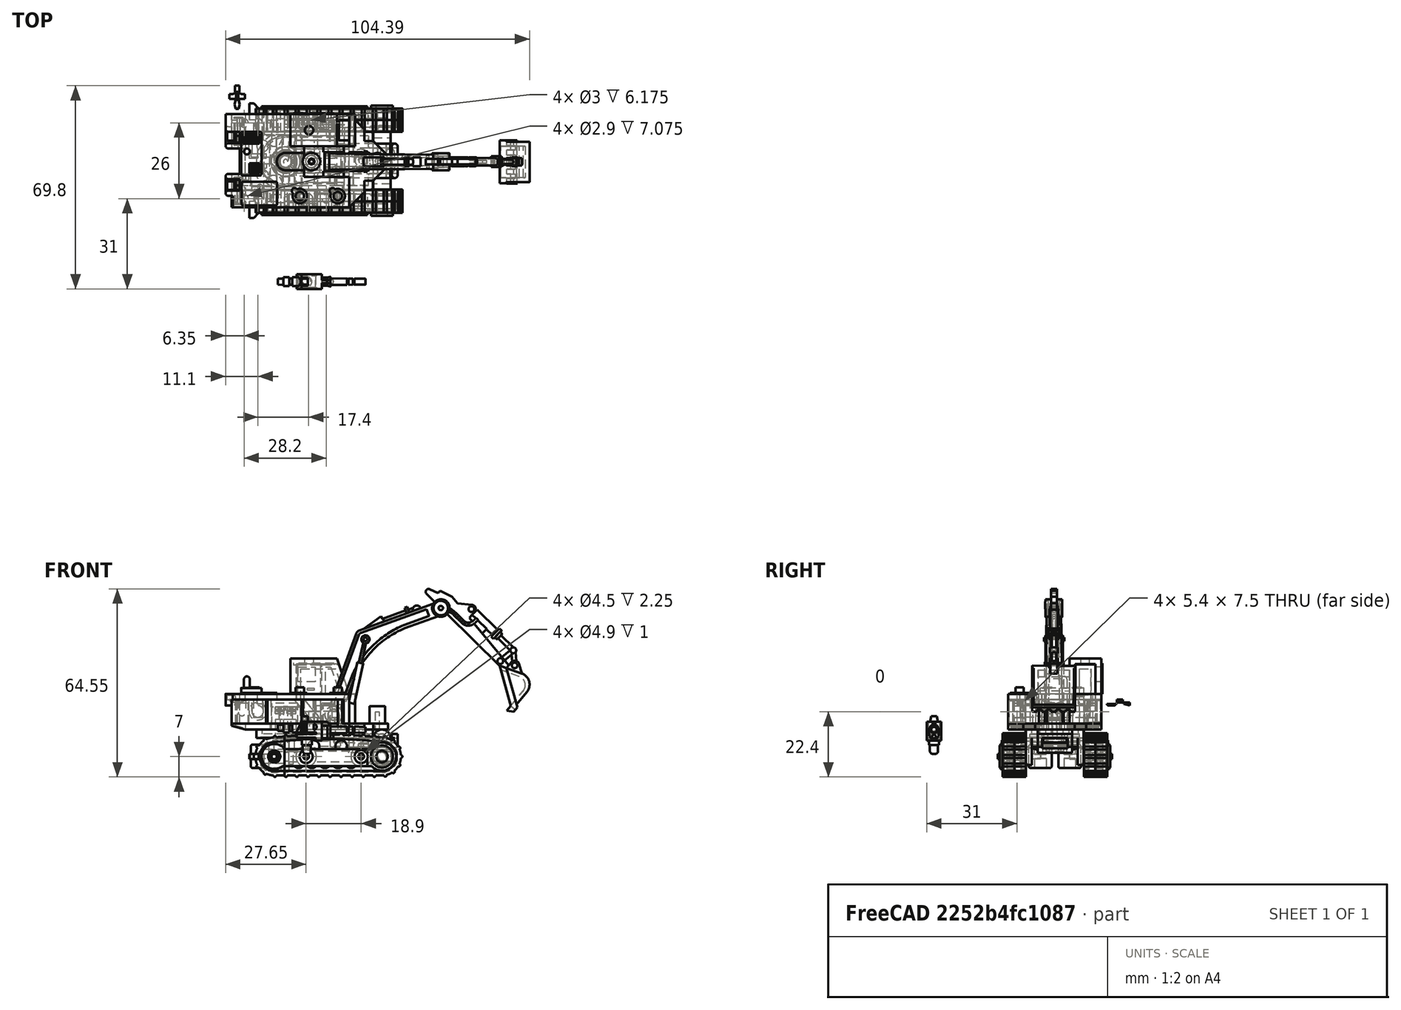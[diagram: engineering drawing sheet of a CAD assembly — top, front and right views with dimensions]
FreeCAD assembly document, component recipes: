
FREECAD ASSEMBLY — COMPONENT RECIPES ("Scavanger")

This assembly document has 15 components, labeled P0..P14 below (a component is one placed body or linked part). 15 of them carry a construction recipe — the FreeCAD feature program that regenerates the part from scratch, quoted from this document or its linked companion documents; the rest are supplied as boundary geometry only. No exploded tour is included for this assembly.
NOTE — this tour is split across 4 documents so each fits a 32k-token context. This is document 1: the component sections continue in the remaining 3 documents, each repeating the header above.
COMPONENT P0 — recipe-attached ("Rear_Torso", modeled in this document).
Construction recipe (the document's own serialized feature program — sketch geometry with constraints, then the solid features built on it; lengths are millimeters unless a unit is written):

FEATURE [Sketcher::SketchObject] Sketch
  ArcFitTolerance = 1e-06
  AttachmentSupport = -> [XY_Plane]
  FullyConstrained = true
  MakeInternals = false
  MapMode = 5
  sketch-geometry (43):
    g0: LineSegment StartX=0 StartY=0 StartZ=0 EndX=44.5 EndY=0 EndZ=0
    g1: LineSegment StartX=44.5 StartY=0 StartZ=0 EndX=44.5 EndY=-11 EndZ=0
    g2: LineSegment StartX=44.5 StartY=-11 StartZ=0 EndX=27 EndY=-11 EndZ=0
    g3: LineSegment StartX=27 StartY=-11 StartZ=0 EndX=27 EndY=-13.25 EndZ=0
    g4: LineSegment StartX=27 StartY=-13.25 StartZ=0 EndX=20.6 EndY=-13.25 EndZ=0
    g5: ArcOfCircle CenterX=20.6 CenterY=-16.25 CenterZ=0 NormalX=0 NormalY=0 NormalZ=1 AngleXU=0 Radius=3 StartAngle=1.5708 EndAngle=4.71239
    g6: LineSegment StartX=20.6 StartY=-19.25 StartZ=0 EndX=27 EndY=-19.25 EndZ=0
    g7: LineSegment StartX=27 StartY=-19.25 StartZ=0 EndX=27 EndY=-21.5 EndZ=0
    g8: LineSegment StartX=27 StartY=-21.5 StartZ=0 EndX=42.5 EndY=-21.5 EndZ=0
    g9: LineSegment StartX=42.5 StartY=-21.5 StartZ=0 EndX=42.5 EndY=-32 EndZ=0
    g10: LineSegment StartX=42.5 StartY=-32 StartZ=0 EndX=2.5 EndY=-32 EndZ=0
    g11: LineSegment StartX=2.5 StartY=-32 StartZ=0 EndX=2.5 EndY=-28 EndZ=0
    g12: LineSegment StartX=2.5 StartY=-28 StartZ=0 EndX=0.875 EndY=-28 EndZ=0
    g13: ArcOfCircle CenterX=0.875 CenterY=-27.125 CenterZ=0 NormalX=0 NormalY=0 NormalZ=1 AngleXU=0 Radius=0.875 StartAngle=1.5708 EndAngle=4.71239
    g14: LineSegment StartX=0.875 StartY=-26.25 StartZ=0 EndX=4.8 EndY=-26.25 EndZ=0
    g15: LineSegment StartX=4.8 StartY=-26.25 StartZ=0 EndX=4.8 EndY=-22.25 EndZ=0
    g16: LineSegment StartX=4.8 StartY=-22.25 StartZ=0 EndX=0.875 EndY=-22.25 EndZ=0
    g17: ArcOfCircle CenterX=0.875 CenterY=-21.375 CenterZ=0 NormalX=0 NormalY=0 NormalZ=1 AngleXU=0 Radius=0.875 StartAngle=1.5708 EndAngle=4.71239
    g18: LineSegment StartX=0.875 StartY=-20.5 StartZ=0 EndX=4.8 EndY=-20.5 EndZ=0
    g19: LineSegment StartX=4.8 StartY=-20.5 StartZ=0 EndX=4.8 EndY=-11.75 EndZ=0
    g20: LineSegment StartX=4.8 StartY=-11.75 StartZ=0 EndX=0.875 EndY=-11.75 EndZ=0
    g21: ArcOfCircle CenterX=0.875 CenterY=-10.875 CenterZ=0 NormalX=0 NormalY=0 NormalZ=1 AngleXU=0 Radius=0.875 StartAngle=1.5708 EndAngle=4.71239
    g22: LineSegment StartX=0.875 StartY=-10 StartZ=0 EndX=4.8 EndY=-10 EndZ=0
    g23: LineSegment StartX=4.8 StartY=-10 StartZ=0 EndX=4.8 EndY=-6 EndZ=0
    g24: LineSegment StartX=4.8 StartY=-6 StartZ=0 EndX=0.875 EndY=-6 EndZ=0
    g25: ArcOfCircle CenterX=0.875 CenterY=-5.125 CenterZ=0 NormalX=0 NormalY=0 NormalZ=1 AngleXU=0 Radius=0.875 StartAngle=3.14159 EndAngle=4.71239
    g26: LineSegment StartX=0 StartY=0 StartZ=0 EndX=0 EndY=-5.125 EndZ=0
    g27: LineSegment [constr] StartX=0.875 StartY=-10 StartZ=0 EndX=0.875 EndY=-10.875 EndZ=0
    g28: LineSegment [constr] StartX=0.875 StartY=-10.875 StartZ=0 EndX=0.875 EndY=-11.75 EndZ=0
    g29: LineSegment [constr] StartX=0.875 StartY=-20.5 StartZ=0 EndX=0.875 EndY=-21.375 EndZ=0
    g30: LineSegment [constr] StartX=0.875 StartY=-21.375 StartZ=0 EndX=0.875 EndY=-22.25 EndZ=0
    g31: LineSegment [constr] StartX=0.875 StartY=-26.25 StartZ=0 EndX=0.875 EndY=-27.125 EndZ=0
    g32: LineSegment [constr] StartX=0.875 StartY=-27.125 StartZ=0 EndX=0.875 EndY=-28 EndZ=0
    g33: LineSegment [constr] StartX=27 StartY=-13.25 StartZ=0 EndX=27 EndY=-19.25 EndZ=0
    g34: LineSegment [constr] StartX=20.6 StartY=-13.25 StartZ=0 EndX=17.6 EndY=-13.25 EndZ=0
    g35: LineSegment [constr] StartX=17.6 StartY=-13.25 StartZ=0 EndX=17.6 EndY=-16.25 EndZ=0
    g36: LineSegment [constr] StartX=20.6 StartY=-13.25 StartZ=0 EndX=20.6 EndY=-19.25 EndZ=0
    g37: LineSegment [constr] StartX=4.8 StartY=-10 StartZ=0 EndX=4.8 EndY=-11.75 EndZ=0
    g38: LineSegment [constr] StartX=4.8 StartY=-20.5 StartZ=0 EndX=4.8 EndY=-22.25 EndZ=0
    g39: LineSegment StartX=42.5 StartY=-2 StartZ=0 EndX=24.3 EndY=-2 EndZ=0
    g40: LineSegment StartX=24.3 StartY=-2 StartZ=0 EndX=24.3 EndY=-9 EndZ=0
    g41: LineSegment StartX=24.3 StartY=-9 StartZ=0 EndX=42.5 EndY=-9 EndZ=0
    g42: LineSegment StartX=42.5 StartY=-9 StartZ=0 EndX=42.5 EndY=-2 EndZ=0
  constraints (123):
    c: Coincident(g0,g-1)
    c: PointOnObject(g0,g-1)
    c: Coincident(g1,g0)
    c: Vertical(g1)
    c: DistanceX(g0,g0) = 44.5
    c: Coincident(g2,g1)
    c: Horizontal(g2)
    c: Coincident(g3,g2)
    c: Vertical(g3)
    c: Coincident(g4,g3)
    c: Horizontal(g4)
    c: Coincident(g5,g4)
    c: Coincident(g6,g5)
    c: Horizontal(g6)
    c: Coincident(g7,g6)
    c: Vertical(g7)
    c: Coincident(g8,g7)
    c: Horizontal(g8)
    c: Coincident(g9,g8)
    c: Vertical(g9)
    c: Coincident(g10,g9)
    c: Horizontal(g10)
    c: Coincident(g11,g10)
    c: Vertical(g11)
    c: Coincident(g12,g11)
    c: Horizontal(g12)
    c: Coincident(g13,g12)
    c: Coincident(g14,g13)
    c: Coincident(g15,g14)
    c: Vertical(g15)
    c: Coincident(g16,g15)
    c: Horizontal(g16)
    c: Coincident(g17,g16)
    c: Coincident(g18,g17)
    c: Horizontal(g18)
    c: Coincident(g19,g18)
    c: Vertical(g19)
    c: Coincident(g20,g19)
    c: Horizontal(g20)
    c: Coincident(g21,g20)
    c: Coincident(g22,g21)
    c: Horizontal(g22)
    c: Coincident(g23,g22)
    c: Vertical(g23)
    c: Coincident(g24,g23)
    c: Horizontal(g24)
    c: Coincident(g25,g24)
    c: PointOnObject(g25,g-2)
    c: Coincident(g26,g0)
    c: Coincident(g26,g25)
    c: DistanceY(g1,g1) = 11
    c: Horizontal(g14)
    c: DistanceX(g10,g10) = 40
    c: Diameter(g5) = 6
    c: Diameter(g17) = 1.75
    c: Diameter(g21) = 1.75
    c: Diameter(g13) = 1.75
    c: Tangent(g17,g-2)
    c: Tangent(g21,g-2)
    c: Diameter(g25) = 1.75
    c: DistanceX(g25,g24) = 0
    c: DistanceY(g25,g25) = 0
    c: Coincident(g27,g21)
    c: Coincident(g27,g21)
    c: Coincident(g28,g21)
    c: Coincident(g28,g20)
    c: Vertical(g27)
    c: Vertical(g28)
    c: Tangent(g13,g-2)
    c: Coincident(g29,g17)
    c: Coincident(g29,g17)
    c: Coincident(g30,g17)
    c: Coincident(g30,g16)
    c: Coincident(g31,g13)
    c: Coincident(g31,g13)
    c: Coincident(g32,g13)
    c: Coincident(g32,g12)
    c: Vertical(g29)
    c: Vertical(g30)
    c: Vertical(g31)
    c: Vertical(g32)
    c: DistanceX(g2,g2) = 17.5
    c: DistanceY(g7,g2) = 10.5
    c: Coincident(g33,g3)
    c: Coincident(g33,g6)
    c: Vertical(g33)
    c: DistanceY(g3,g2) = 2.25
    c: Coincident(g34,g4)
    c: Horizontal(g34)
    c: Tangent(g34,g5)
    c: Coincident(g35,g34)
    c: Tangent(g35,g5) = -1.5708
    c: Vertical(g35)
    c: Coincident(g36,g4)
    c: Coincident(g36,g5)
    c: Vertical(g36)
    c: DistanceX(g35,g1) = 26.9
    c: DistanceX(g8,g8) = 15.5
    c: DistanceY(g9,g9) = 10.5
    c: DistanceY(g11,g11) = 4
    c: Coincident(g37,g22)
    c: Coincident(g37,g19)
    c: Vertical(g37)
    c: Coincident(g38,g18)
    c: Coincident(g38,g15)
    c: Vertical(g38)
    c: DistanceY(g24,g0) = 6
    c: DistanceY(g23,g23) = 4
    c: DistanceY(g15,g15) = 4
    c: DistanceX(g25,g23) = 4.8
    c: DistanceX(g19,g35) = 12.8
    c: Coincident(g39,g40)
    c: Coincident(g40,g41)
    c: Coincident(g41,g42)
    c: Coincident(g42,g39)
    c: Horizontal(g39)
    c: Horizontal(g41)
    c: Vertical(g40)
    c: Vertical(g42)
    c: DistanceX(g39,g0) = 2
    c: DistanceY(g39,g0) = 2
    c: DistanceY(g1,g41) = 2
    c: DistanceX(g39,g39) = 18.2
FEATURE [PartDesign::Pad] Pad
  Direction = (0,0,1)
  Length = 2
  Length2 = 10
  Profile = -> Sketch
  ReferenceAxis = -> Sketch [N_Axis]
  Refine = true
  Suppressed = false
  Type = 0
FEATURE [Sketcher::SketchObject] Sketch001
  ArcFitTolerance = 1e-06
  AttachmentSupport = -> [Pad]
  ExternalGeometry = -> [Pad]
  FullyConstrained = true
  MakeInternals = false
  MapMode = 5
  Placement = pos=(0,0,0) rot=(0,0.707107,0.707107;3.14159rad)
  sketch-geometry (4):
    g0: LineSegment StartX=-42.5 StartY=2 StartZ=0 EndX=-38.2 EndY=14.2 EndZ=0
    g1: LineSegment StartX=-38.2 StartY=14.2 StartZ=0 EndX=-22.3 EndY=14.2 EndZ=0
    g2: LineSegment StartX=-22.3 StartY=14.2 StartZ=0 EndX=-22.3 EndY=2 EndZ=0
    g3: LineSegment StartX=-22.3 StartY=2 StartZ=0 EndX=-42.5 EndY=2 EndZ=0
  constraints (12):
    c: Coincident(g0,g-5)
    c: Coincident(g1,g0)
    c: Horizontal(g1)
    c: DistanceY(g-6,g1) = 12.2
    c: DistanceX(g1,g1) = 15.9
    c: Coincident(g2,g1)
    c: PointOnObject(g2,g-3)
    c: Vertical(g2)
    c: DistanceX(g0,g2) = 20.2
    c: DistanceX(g-6,g2) = 2
    c: Coincident(g3,g2)
    c: Coincident(g3,g0)
FEATURE [PartDesign::Pad] Pad001
  BaseFeature = -> Pad
  Direction = (0,1,-2e-16)
  Length = 2
  Length2 = 10
  Profile = -> Sketch001
  ReferenceAxis = -> Sketch001 [N_Axis]
  Refine = true
  Reversed = true
  Suppressed = false
  Type = 0
FEATURE [Sketcher::SketchObject] Sketch002
  ArcFitTolerance = 1e-06
  AttachmentSupport = -> [Pad001]
  ExternalGeometry = -> [Pad001]
  FullyConstrained = true
  MakeInternals = false
  MapMode = 5
  Placement = pos=(0,-11,0) rot=(1,0,0;1.5708rad)
  sketch-geometry (4):
    g0: LineSegment StartX=22.3 StartY=2 StartZ=0 EndX=42.5 EndY=2 EndZ=0
    g1: LineSegment StartX=42.5 StartY=2 StartZ=0 EndX=38.2 EndY=14.2 EndZ=0
    g2: LineSegment StartX=38.2 StartY=14.2 StartZ=0 EndX=22.3 EndY=14.2 EndZ=0
    g3: LineSegment StartX=22.3 StartY=14.2 StartZ=0 EndX=22.3 EndY=2 EndZ=0
  constraints (8):
    c: Coincident(g0,g-4)
    c: Coincident(g0,g-3)
    c: Coincident(g1,g0)
    c: Coincident(g1,g-5)
    c: Coincident(g2,g1)
    c: Coincident(g2,g-5)
    c: Coincident(g3,g2)
    c: Coincident(g3,g0)
FEATURE [PartDesign::Pad] Pad002
  BaseFeature = -> Pad001
  Direction = (0,-1,2e-16)
  Length = 2
  Length2 = 10
  Profile = -> Sketch002
  ReferenceAxis = -> Sketch002 [N_Axis]
  Refine = true
  Reversed = true
  Suppressed = false
  Type = 0
FEATURE [Sketcher::SketchObject] Sketch003
  ArcFitTolerance = 1e-06
  AttachmentSupport = -> [Pad002]
  ExternalGeometry = -> [Pad002]
  FullyConstrained = true
  MakeInternals = false
  MapMode = 5
  Placement = pos=(0,0,2) rot=(0,0,1;0rad)
  sketch-geometry (4):
    g0: LineSegment StartX=24.3 StartY=-2 StartZ=0 EndX=22.3 EndY=-2 EndZ=0
    g1: LineSegment StartX=22.3 StartY=-2 StartZ=0 EndX=22.3 EndY=-9 EndZ=0
    g2: LineSegment StartX=22.3 StartY=-9 StartZ=0 EndX=24.3 EndY=-9 EndZ=0
    g3: LineSegment StartX=24.3 StartY=-9 StartZ=0 EndX=24.3 EndY=-2 EndZ=0
  constraints (10):
    c: Coincident(g0,g1)
    c: Coincident(g1,g2)
    c: Coincident(g2,g3)
    c: Coincident(g3,g0)
    c: Horizontal(g0)
    c: Horizontal(g2)
    c: Vertical(g1)
    c: Vertical(g3)
    c: Coincident(g0,g-4)
    c: Coincident(g1,g-5)
FEATURE [PartDesign::Pad] Pad003
  BaseFeature = -> Pad002
  Direction = (0,0,1)
  Length = 12.2
  Length2 = 10
  Profile = -> Sketch003
  ReferenceAxis = -> Sketch003 [N_Axis]
  Refine = true
  Suppressed = false
  Type = 0
FEATURE [Sketcher::SketchObject] Sketch004
  ArcFitTolerance = 1e-06
  AttachmentSupport = -> [Pad003]
  ExternalGeometry = -> [Pad003]
  FullyConstrained = true
  MakeInternals = false
  MapMode = 5
  Placement = pos=(0,-2,0) rot=(1,0,0;1.5708rad)
  sketch-geometry (4):
    g0: LineSegment StartX=24.3 StartY=14.2 StartZ=0 EndX=38.2 EndY=14.2 EndZ=0
    g1: LineSegment StartX=38.2 StartY=14.2 StartZ=0 EndX=38.9049 EndY=12.2 EndZ=0
    g2: LineSegment StartX=38.9049 StartY=12.2 StartZ=0 EndX=24.3 EndY=12.2 EndZ=0
    g3: LineSegment StartX=24.3 StartY=12.2 StartZ=0 EndX=24.3 EndY=14.2 EndZ=0
  constraints (10):
    c: Coincident(g0,g-3)
    c: Coincident(g0,g-4)
    c: Coincident(g1,g0)
    c: PointOnObject(g1,g-4)
    c: Coincident(g2,g1)
    c: Horizontal(g2)
    c: Coincident(g3,g2)
    c: Vertical(g3)
    c: Coincident(g3,g0)
    c: DistanceY(g3,g3) = 2
FEATURE [PartDesign::Pad] Pad004
  BaseFeature = -> Pad003
  Direction = (0,-1,2e-16)
  Length = 7
  Length2 = 10
  Profile = -> Sketch004
  ReferenceAxis = -> Sketch004 [N_Axis]
  Refine = true
  Suppressed = false
  Type = 0
FEATURE [Sketcher::SketchObject] Sketch005
  ArcFitTolerance = 1e-06
  AttachmentSupport = -> [Pad004]
  ExternalGeometry = -> [Pad004]
  FullyConstrained = true
  MakeInternals = false
  MapMode = 5
  Placement = pos=(0,0,0) rot=(1,0,0;3.14159rad)
  sketch-geometry (17):
    g0: ArcOfCircle CenterX=0.875 CenterY=27.125 CenterZ=0 NormalX=0 NormalY=0 NormalZ=1 AngleXU=0 Radius=0.875 StartAngle=1.5708 EndAngle=3.14159
    g1: ArcOfCircle CenterX=0.875 CenterY=21.375 CenterZ=0 NormalX=0 NormalY=0 NormalZ=1 AngleXU=0 Radius=0.875 StartAngle=3.14159 EndAngle=4.71239
    g2: LineSegment [constr] StartX=0.875 StartY=21.375 StartZ=0 EndX=-1e-16 EndY=21.375 EndZ=0
    g3: LineSegment [constr] StartX=0.875 StartY=27.125 StartZ=0 EndX=0 EndY=27.125 EndZ=0
    g4: LineSegment StartX=0 StartY=27.125 StartZ=0 EndX=-1e-16 EndY=21.375 EndZ=0
    g5: LineSegment StartX=0.875 StartY=20.5 StartZ=0 EndX=2 EndY=20.5 EndZ=0
    g6: LineSegment StartX=2 StartY=20.5 StartZ=0 EndX=2 EndY=28 EndZ=0
    g7: LineSegment StartX=2 StartY=28 StartZ=0 EndX=0.875 EndY=28 EndZ=0
    g8: ArcOfCircle CenterX=0.875 CenterY=10.875 CenterZ=0 NormalX=0 NormalY=0 NormalZ=1 AngleXU=0 Radius=0.875 StartAngle=1.5708 EndAngle=3.14159
    g9: LineSegment StartX=2 StartY=4.25 StartZ=0 EndX=2 EndY=11.75 EndZ=0
    g10: LineSegment StartX=2 StartY=11.75 StartZ=0 EndX=0.875 EndY=11.75 EndZ=0
    g11: LineSegment [constr] StartX=0.875 StartY=10.875 StartZ=0 EndX=1.5096e-12 EndY=10.875 EndZ=0
    g12: LineSegment StartX=1.5096e-12 StartY=10.875 StartZ=0 EndX=1.5096e-12 EndY=5.125 EndZ=0
    g13: ArcOfCircle CenterX=0.875 CenterY=5.125 CenterZ=0 NormalX=0 NormalY=0 NormalZ=1 AngleXU=0 Radius=0.875 StartAngle=3.14159 EndAngle=4.71239
    g14: LineSegment [constr] StartX=0.875 StartY=5.125 StartZ=0 EndX=1.5096e-12 EndY=5.125 EndZ=0
    g15: LineSegment [constr] StartX=0.875 StartY=5.125 StartZ=0 EndX=0.875 EndY=4.25 EndZ=0
    g16: LineSegment StartX=0.875 StartY=4.25 StartZ=0 EndX=2 EndY=4.25 EndZ=0
  constraints (44):
    c: Tangent(g0,g-3) = -1.5708
    c: PointOnObject(g0,g-3)
    c: Tangent(g1,g-4) = -1.5708
    c: PointOnObject(g1,g-4)
    c: Coincident(g2,g1)
    c: Coincident(g2,g1)
    c: Horizontal(g2)
    c: Coincident(g3,g0)
    c: Coincident(g3,g0)
    c: Horizontal(g3)
    c: Coincident(g4,g0)
    c: Coincident(g4,g1)
    c: Coincident(g5,g1)
    c: Horizontal(g5)
    c: Coincident(g6,g5)
    c: Vertical(g6)
    c: Coincident(g7,g6)
    c: Coincident(g7,g0)
    c: Horizontal(g7)
    c: Tangent(g8,g-5) = -1.5708
    c: PointOnObject(g8,g-5)
    c: Vertical(g9)
    c: Coincident(g10,g9)
    c: Coincident(g10,g8)
    c: Horizontal(g10)
    c: Coincident(g11,g8)
    c: Coincident(g11,g8)
    c: Coincident(g12,g8)
    c: Coincident(g12,g-6)
    c: Vertical(g12)
    c: Coincident(g13,g12)
    c: Coincident(g14,g-6)
    c: Coincident(g14,g12)
    c: Coincident(g15,g14)
    c: Coincident(g15,g13)
    c: Vertical(g15)
    c: Radius(g-6) = 0.875
    c: Radius(g-5) = 0.875
    c: Coincident(g13,g14)
    c: Coincident(g16,g13)
    c: Coincident(g16,g9)
    c: Horizontal(g16)
    c: DistanceX(g0,g6) = 2
    c: DistanceX(g12,g9) = 2
FEATURE [PartDesign::Pad] Pad005
  BaseFeature = -> Pad004
  Direction = (0,0,-1)
  Length = 2
  Length2 = 10
  Profile = -> Sketch005
  ReferenceAxis = -> Sketch005 [N_Axis]
  Refine = true
  Suppressed = false
  Type = 0
FEATURE [Sketcher::SketchObject] Sketch006
  ArcFitTolerance = 1e-06
  AttachmentSupport = -> [Pad005]
  FullyConstrained = true
  MakeInternals = false
  MapMode = 5
  Placement = pos=(0,0,2) rot=(0,0,1;0rad)
  sketch-geometry (12):
    g0: LineSegment StartX=5.3 StartY=-6.5 StartZ=0 EndX=5.3 EndY=-20.5 EndZ=0
    g1: LineSegment StartX=5.8 StartY=-21 StartZ=0 EndX=11.8 EndY=-21 EndZ=0
    g2: LineSegment StartX=12.3 StartY=-20.5 StartZ=0 EndX=12.3 EndY=-6.5 EndZ=0
    g3: LineSegment StartX=11.8 StartY=-6 StartZ=0 EndX=5.8 EndY=-6 EndZ=0
    g4: ArcOfCircle CenterX=5.8 CenterY=-6.5 CenterZ=0 NormalX=0 NormalY=0 NormalZ=1 AngleXU=0 Radius=0.5 StartAngle=1.5708 EndAngle=3.14159
    g5: GeomPoint [constr] X=5.3 Y=-6 Z=0
    g6: ArcOfCircle CenterX=11.8 CenterY=-6.5 CenterZ=0 NormalX=0 NormalY=0 NormalZ=1 AngleXU=0 Radius=0.5 StartAngle=0 EndAngle=1.5708
    g7: GeomPoint [constr] X=12.3 Y=-6 Z=0
    g8: ArcOfCircle CenterX=11.8 CenterY=-20.5 CenterZ=0 NormalX=0 NormalY=0 NormalZ=1 AngleXU=0 Radius=0.5 StartAngle=4.71239 EndAngle=6.28319
    g9: GeomPoint [constr] X=12.3 Y=-21 Z=0
    g10: ArcOfCircle CenterX=5.8 CenterY=-20.5 CenterZ=0 NormalX=0 NormalY=0 NormalZ=1 AngleXU=0 Radius=0.5 StartAngle=3.14159 EndAngle=4.71239
    g11: GeomPoint [constr] X=5.3 Y=-21 Z=0
  constraints (28):
    c: Vertical(g0)
    c: Vertical(g2)
    c: Horizontal(g1)
    c: Horizontal(g3)
    c: PointOnObject(g5,g0)
    c: PointOnObject(g5,g3)
    c: Tangent(g0,g4) = -1.5708
    c: Tangent(g3,g4) = -1.5708
    c: PointOnObject(g7,g2)
    c: PointOnObject(g7,g3)
    c: Tangent(g2,g6) = -1.5708
    c: Tangent(g3,g6) = -1.5708
    c: PointOnObject(g9,g1)
    c: PointOnObject(g9,g2)
    c: Tangent(g1,g8) = -1.5708
    c: Tangent(g2,g8) = -1.5708
    c: PointOnObject(g11,g0)
    c: PointOnObject(g11,g1)
    c: Tangent(g0,g10) = -1.5708
    c: Tangent(g1,g10) = -1.5708
    c: Radius(g4) = 0.5
    c: Radius(g6) = 0.5
    c: Radius(g10) = 0.5
    c: Radius(g8) = 0.5
    c: DistanceY(g1,g3) = 15
    c: DistanceX(g0,g2) = 7
    c: DistanceY(g3,g-1) = 6
    c: DistanceX(g-1,g0) = 5.3
FEATURE [PartDesign::Pad] Pad006
  BaseFeature = -> Pad005
  Direction = (0,0,1)
  Length = 2
  Length2 = 10
  Profile = -> Sketch006
  ReferenceAxis = -> Sketch006 [N_Axis]
  Refine = true
  Suppressed = false
  Type = 0
FEATURE [Sketcher::SketchObject] Sketch007
  ArcFitTolerance = 1e-06
  AttachmentSupport = -> [Pad006]
  ExternalGeometry = -> [Pad006]
  FullyConstrained = true
  MakeInternals = false
  MapMode = 5
  Placement = pos=(0,0,4) rot=(0,0,1;0rad)
  sketch-geometry (4):
    g0: Circle CenterX=7.3 CenterY=-12.8 CenterZ=0 NormalX=0 NormalY=0 NormalZ=1 AngleXU=0 Radius=1
    g1: LineSegment [constr] StartX=7.3 StartY=-12.8 StartZ=0 EndX=7.3 EndY=-13.8 EndZ=0
    g2: LineSegment [constr] StartX=7.3 StartY=-12.8 StartZ=0 EndX=7.3 EndY=-11.8 EndZ=0
    g3: LineSegment [constr] StartX=7.3 StartY=-12.8 StartZ=0 EndX=6.3 EndY=-12.8 EndZ=0
  constraints (12):
    c: Diameter(g0) = 2
    c: Coincident(g1,g0)
    c: PointOnObject(g1,g0)
    c: Vertical(g1)
    c: Coincident(g2,g0)
    c: PointOnObject(g2,g0)
    c: Vertical(g2)
    c: DistanceY(g2,g-1) = 11.8
    c: Coincident(g3,g0)
    c: PointOnObject(g3,g0)
    c: Horizontal(g3)
    c: DistanceX(g-3,g3) = 1
FEATURE [PartDesign::Pad] Pad007
  BaseFeature = -> Pad006
  Direction = (0,0,1)
  Length = 4
  Length2 = 10
  Profile = -> Sketch007
  ReferenceAxis = -> Sketch007 [N_Axis]
  Refine = true
  Suppressed = false
  Type = 0
FEATURE [PartDesign::Fillet] Fillet
  Base = -> Pad007 [Edge171]
  BaseFeature = -> Pad007
  Radius = 1
  Refine = true
  SupportTransform = false
  Suppressed = false
  UseAllEdges = false
FEATURE [Sketcher::SketchObject] Sketch008
  ArcFitTolerance = 1e-06
  AttachmentSupport = -> [Fillet]
  ExternalGeometry = -> [Fillet]
  FullyConstrained = true
  MakeInternals = false
  MapMode = 5
  Placement = pos=(0,0,4) rot=(0,0,1;0rad)
  sketch-geometry (16):
    g0: LineSegment StartX=11.6 StartY=-6.7 StartZ=0 EndX=6 EndY=-6.7 EndZ=0
    g1: LineSegment StartX=6 StartY=-6.7 StartZ=0 EndX=6 EndY=-10.1 EndZ=0
    g2: LineSegment StartX=6 StartY=-10.1 StartZ=0 EndX=11.6 EndY=-10.1 EndZ=0
    g3: LineSegment StartX=11.6 StartY=-10.1 StartZ=0 EndX=11.6 EndY=-6.7 EndZ=0
    g4: LineSegment StartX=11.4 StartY=-6.9 StartZ=0 EndX=6.2 EndY=-6.9 EndZ=0
    g5: LineSegment StartX=6.2 StartY=-6.9 StartZ=0 EndX=6.2 EndY=-9.9 EndZ=0
    g6: LineSegment StartX=6.2 StartY=-9.9 StartZ=0 EndX=11.4 EndY=-9.9 EndZ=0
    g7: LineSegment StartX=11.4 StartY=-9.9 StartZ=0 EndX=11.4 EndY=-6.9 EndZ=0
    g8: LineSegment StartX=11.6 StartY=-16.9 StartZ=0 EndX=8.2 EndY=-16.9 EndZ=0
    g9: LineSegment StartX=8.2 StartY=-16.9 StartZ=0 EndX=8.2 EndY=-20.3 EndZ=0
    g10: LineSegment StartX=8.2 StartY=-20.3 StartZ=0 EndX=11.6 EndY=-20.3 EndZ=0
    g11: LineSegment StartX=11.6 StartY=-20.3 StartZ=0 EndX=11.6 EndY=-16.9 EndZ=0
    g12: LineSegment StartX=11.4 StartY=-17.1 StartZ=0 EndX=8.4 EndY=-17.1 EndZ=0
    g13: LineSegment StartX=8.4 StartY=-17.1 StartZ=0 EndX=8.4 EndY=-20.1 EndZ=0
    g14: LineSegment StartX=8.4 StartY=-20.1 StartZ=0 EndX=11.4 EndY=-20.1 EndZ=0
    g15: LineSegment StartX=11.4 StartY=-20.1 StartZ=0 EndX=11.4 EndY=-17.1 EndZ=0
  constraints (50):
    c: Coincident(g0,g1)
    c: Coincident(g1,g2)
    c: Coincident(g2,g3)
    c: Coincident(g3,g0)
    c: Horizontal(g0)
    c: Horizontal(g2)
    c: Vertical(g1)
    c: Vertical(g3)
    c: Coincident(g4,g5)
    c: Coincident(g5,g6)
    c: Coincident(g6,g7)
    c: Coincident(g7,g4)
    c: Horizontal(g4)
    c: Horizontal(g6)
    c: Vertical(g5)
    c: Vertical(g7)
    c: Coincident(g8,g9)
    c: Coincident(g9,g10)
    c: Coincident(g10,g11)
    c: Coincident(g11,g8)
    c: Horizontal(g8)
    c: Horizontal(g10)
    c: Vertical(g9)
    c: Vertical(g11)
    c: Coincident(g12,g13)
    c: Coincident(g13,g14)
    c: Coincident(g14,g15)
    c: Coincident(g15,g12)
    c: Horizontal(g12)
    c: Horizontal(g14)
    c: Vertical(g13)
    c: Vertical(g15)
    c: DistanceX(g8,g8) = 3.4
    c: DistanceY(g9,g9) = 3.4
    c: DistanceX(g8,g12) = 0.2
    c: DistanceX(g12,g8) = 0.2
    c: DistanceY(g12,g8) = 0.2
    c: DistanceY(g9,g13) = 0.2
    c: DistanceX(g6,g2) = 0.2
    c: DistanceX(g1,g5) = 0.2
    c: DistanceY(g1,g5) = 0.2
    c: DistanceY(g4,g0) = 0.2
    c: DistanceX(g0,g0) = 5.6
    c: DistanceY(g1,g1) = 3.4
    c: DistanceX(g-4,g-3) = 7
    c: DistanceX(g-4,g0) = 0.7
    c: DistanceY(g0,g-5) = 0.7
    c: DistanceY(g-6,g10) = 0.7
    c: DistanceX(g10,g-3) = 0.7
    c: DistanceX(g0,g-3) = 0.7
FEATURE [PartDesign::Pad] Pad008
  BaseFeature = -> Fillet
  Direction = (0,0,1)
  Length = 0.3
  Length2 = 10
  Profile = -> Sketch008
  ReferenceAxis = -> Sketch008 [N_Axis]
  Refine = true
  Suppressed = false
  Type = 0
FEATURE [Sketcher::SketchObject] Sketch009
  ArcFitTolerance = 1e-06
  AttachmentSupport = -> [Pad008]
  ExternalGeometry = -> [Pad008]
  FullyConstrained = true
  MakeInternals = false
  MapMode = 5
  Placement = pos=(0,0,4) rot=(0,0,1;0rad)
  sketch-geometry (197):
    g0: LineSegment [constr] StartX=11.4 StartY=-6.9 StartZ=0 EndX=8.4 EndY=-9.9 EndZ=0
    g1: LineSegment [constr] StartX=10.1 StartY=-6.9 StartZ=0 EndX=7.1 EndY=-9.9 EndZ=0
    g2: LineSegment [constr] StartX=8.8 StartY=-6.9 StartZ=0 EndX=6.2 EndY=-9.5 EndZ=0
    g3: LineSegment [constr] StartX=7.5 StartY=-6.9 StartZ=0 EndX=6.2 EndY=-8.2 EndZ=0
    g4: LineSegment [constr] StartX=11.4 StartY=-8.2 StartZ=0 EndX=9.7 EndY=-9.9 EndZ=0
    g5: LineSegment [constr] StartX=11.4 StartY=-9.5 StartZ=0 EndX=11 EndY=-9.9 EndZ=0
    g6: LineSegment [constr] StartX=6.2 StartY=-6.9 StartZ=0 EndX=9.2 EndY=-9.9 EndZ=0
    g7: LineSegment [constr] StartX=7.5 StartY=-6.9 StartZ=0 EndX=10.5 EndY=-9.9 EndZ=0
    g8: LineSegment [constr] StartX=8.8 StartY=-6.9 StartZ=0 EndX=11.4 EndY=-9.5 EndZ=0
    g9: LineSegment [constr] StartX=10.1 StartY=-6.9 StartZ=0 EndX=11.4 EndY=-8.2 EndZ=0
    g10: LineSegment [constr] StartX=6.2 StartY=-8.2 StartZ=0 EndX=7.9 EndY=-9.9 EndZ=0
    g11: LineSegment [constr] StartX=6.2 StartY=-9.5 StartZ=0 EndX=6.6 EndY=-9.9 EndZ=0
    g12: LineSegment StartX=11.4 StartY=-9.65 StartZ=0 EndX=8.65 EndY=-6.9 EndZ=0
    g13: LineSegment StartX=11.4 StartY=-9.35 StartZ=0 EndX=8.95 EndY=-6.9 EndZ=0
    g14: LineSegment StartX=11.4 StartY=-8.05 StartZ=0 EndX=10.25 EndY=-6.9 EndZ=0
    g15: LineSegment StartX=11.4 StartY=-8.35 StartZ=0 EndX=9.95 EndY=-6.9 EndZ=0
    g16: LineSegment StartX=7.65 StartY=-6.9 StartZ=0 EndX=10.65 EndY=-9.9 EndZ=0
    g17: LineSegment StartX=7.35 StartY=-6.9 StartZ=0 EndX=10.35 EndY=-9.9 EndZ=0
    g18: LineSegment StartX=6.35 StartY=-6.9 StartZ=0 EndX=9.35 EndY=-9.9 EndZ=0
    g19: LineSegment StartX=6.2 StartY=-7.05 StartZ=0 EndX=9.05 EndY=-9.9 EndZ=0
    g20: LineSegment StartX=6.2 StartY=-8.05 StartZ=0 EndX=8.05 EndY=-9.9 EndZ=0
    g21: LineSegment StartX=6.2 StartY=-8.35 StartZ=0 EndX=7.75 EndY=-9.9 EndZ=0
    g22: LineSegment StartX=6.75 StartY=-9.9 StartZ=0 EndX=6.2 EndY=-9.35 EndZ=0
    g23: LineSegment StartX=6.45 StartY=-9.9 StartZ=0 EndX=6.2 EndY=-9.65 EndZ=0
    g24: LineSegment StartX=10.25 StartY=-6.9 StartZ=0 EndX=9.95 EndY=-6.9 EndZ=0
    g25: LineSegment StartX=8.95 StartY=-6.9 StartZ=0 EndX=8.65 EndY=-6.9 EndZ=0
    g26: LineSegment StartX=7.65 StartY=-6.9 StartZ=0 EndX=7.35 EndY=-6.9 EndZ=0
    g27: LineSegment StartX=6.35 StartY=-6.9 StartZ=0 EndX=6.2 EndY=-6.9 EndZ=0
    g28: LineSegment StartX=6.2 StartY=-6.9 StartZ=0 EndX=6.2 EndY=-7.05 EndZ=0
    g29: LineSegment StartX=6.2 StartY=-8.05 StartZ=0 EndX=6.2 EndY=-8.35 EndZ=0
    g30: LineSegment StartX=6.2 StartY=-9.35 StartZ=0 EndX=6.2 EndY=-9.65 EndZ=0
    g31: LineSegment StartX=6.45 StartY=-9.9 StartZ=0 EndX=6.75 EndY=-9.9 EndZ=0
    g32: LineSegment StartX=7.75 StartY=-9.9 StartZ=0 EndX=8.05 EndY=-9.9 EndZ=0
    g33: LineSegment StartX=9.05 StartY=-9.9 StartZ=0 EndX=9.35 EndY=-9.9 EndZ=0
    g34: LineSegment StartX=10.35 StartY=-9.9 StartZ=0 EndX=10.65 EndY=-9.9 EndZ=0
    g35: LineSegment StartX=11.4 StartY=-9.65 StartZ=0 EndX=11.4 EndY=-9.35 EndZ=0
    g36: LineSegment StartX=11.4 StartY=-8.35 StartZ=0 EndX=11.4 EndY=-8.05 EndZ=0
    g37: LineSegment StartX=9.88358 StartY=-8.275 StartZ=0 EndX=9.525 EndY=-8.63358 EndZ=0
    g38: LineSegment StartX=10.025 StartY=-8.41642 StartZ=0 EndX=9.66642 EndY=-8.775 EndZ=0
    g39: LineSegment StartX=10.5336 StartY=-7.625 StartZ=0 EndX=10.175 EndY=-7.98358 EndZ=0
    g40: LineSegment StartX=10.675 StartY=-7.76642 StartZ=0 EndX=10.3164 EndY=-8.125 EndZ=0
    g41: LineSegment StartX=11.1856 StartY=-6.97295 StartZ=0 EndX=10.825 EndY=-7.33358 EndZ=0
    g42: LineSegment StartX=11.327 StartY=-7.11438 StartZ=0 EndX=10.9664 EndY=-7.475 EndZ=0
    g43: LineSegment StartX=9.88358 StartY=-6.975 StartZ=0 EndX=9.525 EndY=-7.33358 EndZ=0
    g44: LineSegment StartX=10.025 StartY=-7.11642 StartZ=0 EndX=9.66642 EndY=-7.475 EndZ=0
    g45: LineSegment StartX=9.23358 StartY=-7.625 StartZ=0 EndX=8.875 EndY=-7.98358 EndZ=0
    g46: LineSegment StartX=9.375 StartY=-7.76642 StartZ=0 EndX=9.01642 EndY=-8.125 EndZ=0
    g47: LineSegment StartX=8.58358 StartY=-8.275 StartZ=0 EndX=8.225 EndY=-8.63358 EndZ=0
    g48: LineSegment StartX=8.725 StartY=-8.41642 StartZ=0 EndX=8.36642 EndY=-8.775 EndZ=0
    g49: LineSegment StartX=9.23358 StartY=-8.925 StartZ=0 EndX=8.875 EndY=-9.28358 EndZ=0
    g50: LineSegment StartX=9.375 StartY=-9.06642 StartZ=0 EndX=9.01642 EndY=-9.425 EndZ=0
    g51: LineSegment StartX=9.88358 StartY=-9.575 StartZ=0 EndX=9.55858 EndY=-9.9 EndZ=0
    g52: LineSegment StartX=10.025 StartY=-9.71642 StartZ=0 EndX=9.84142 EndY=-9.9 EndZ=0
    g53: LineSegment StartX=8.58358 StartY=-9.575 StartZ=0 EndX=8.25858 EndY=-9.9 EndZ=0
    g54: LineSegment StartX=8.725 StartY=-9.71642 StartZ=0 EndX=8.54142 EndY=-9.9 EndZ=0
    g55: LineSegment StartX=7.28358 StartY=-9.575 StartZ=0 EndX=6.95858 EndY=-9.9 EndZ=0
    g56: LineSegment StartX=7.425 StartY=-9.71642 StartZ=0 EndX=7.24142 EndY=-9.9 EndZ=0
    g57: LineSegment StartX=6.63358 StartY=-8.925 StartZ=0 EndX=6.275 EndY=-9.28358 EndZ=0
    g58: LineSegment StartX=6.775 StartY=-9.06642 StartZ=0 EndX=6.41642 EndY=-9.425 EndZ=0
    g59: LineSegment StartX=7.28358 StartY=-8.275 StartZ=0 EndX=6.925 EndY=-8.63358 EndZ=0
    g60: LineSegment StartX=7.425 StartY=-8.41642 StartZ=0 EndX=7.06642 EndY=-8.775 EndZ=0
    g61: LineSegment StartX=7.93358 StartY=-7.625 StartZ=0 EndX=7.575 EndY=-7.98358 EndZ=0
    g62: LineSegment StartX=8.075 StartY=-7.76642 StartZ=0 EndX=7.71642 EndY=-8.125 EndZ=0
    g63: LineSegment StartX=8.58358 StartY=-6.975 StartZ=0 EndX=8.225 EndY=-7.33358 EndZ=0
    g64: LineSegment StartX=8.725 StartY=-7.11642 StartZ=0 EndX=8.36642 EndY=-7.475 EndZ=0
    g65: LineSegment StartX=7.28358 StartY=-6.975 StartZ=0 EndX=6.925 EndY=-7.33358 EndZ=0
    g66: LineSegment StartX=7.425 StartY=-7.11642 StartZ=0 EndX=7.06642 EndY=-7.475 EndZ=0
    g67: LineSegment StartX=6.63358 StartY=-7.625 StartZ=0 EndX=6.275 EndY=-7.98358 EndZ=0
    g68: LineSegment StartX=6.775 StartY=-7.76642 StartZ=0 EndX=6.41642 EndY=-8.125 EndZ=0
    g69: LineSegment StartX=7.93358 StartY=-8.925 StartZ=0 EndX=7.575 EndY=-9.28358 EndZ=0
    g70: LineSegment StartX=8.075 StartY=-9.06642 StartZ=0 EndX=7.71642 EndY=-9.425 EndZ=0
    g71: LineSegment StartX=10.5336 StartY=-8.925 StartZ=0 EndX=10.175 EndY=-9.28358 EndZ=0
    g72: LineSegment StartX=10.675 StartY=-9.06642 StartZ=0 EndX=10.3164 EndY=-9.425 EndZ=0
    g73: LineSegment StartX=11.1836 StartY=-8.275 StartZ=0 EndX=10.825 EndY=-8.63358 EndZ=0
    g74: LineSegment StartX=11.325 StartY=-8.41642 StartZ=0 EndX=10.9664 EndY=-8.775 EndZ=0
    g75: LineSegment StartX=10.9664 StartY=-8.775 StartZ=0 EndX=10.825 EndY=-8.63358 EndZ=0
    g76: LineSegment StartX=11.325 StartY=-8.41642 StartZ=0 EndX=11.1836 EndY=-8.275 EndZ=0
    g77: LineSegment StartX=11.327 StartY=-7.11438 StartZ=0 EndX=11.1856 EndY=-6.97295 EndZ=0
    g78: LineSegment StartX=10.9664 StartY=-7.475 StartZ=0 EndX=10.825 EndY=-7.33358 EndZ=0
    g79: LineSegment StartX=10.675 StartY=-7.76642 StartZ=0 EndX=10.5336 EndY=-7.625 EndZ=0
    g80: LineSegment StartX=10.3164 StartY=-8.125 StartZ=0 EndX=10.175 EndY=-7.98358 EndZ=0
    g81: LineSegment StartX=10.025 StartY=-7.11642 StartZ=0 EndX=9.88358 EndY=-6.975 EndZ=0
    g82: LineSegment StartX=9.66642 StartY=-7.475 StartZ=0 EndX=9.525 EndY=-7.33358 EndZ=0
    g83: LineSegment StartX=9.375 StartY=-7.76642 StartZ=0 EndX=9.23358 EndY=-7.625 EndZ=0
    g84: LineSegment StartX=9.01642 StartY=-8.125 StartZ=0 EndX=8.875 EndY=-7.98358 EndZ=0
    g85: LineSegment StartX=8.36642 StartY=-7.475 StartZ=0 EndX=8.225 EndY=-7.33358 EndZ=0
    g86: LineSegment StartX=8.725 StartY=-7.11642 StartZ=0 EndX=8.58358 EndY=-6.975 EndZ=0
    g87: LineSegment StartX=8.075 StartY=-7.76642 StartZ=0 EndX=7.93358 EndY=-7.625 EndZ=0
    g88: LineSegment StartX=7.425 StartY=-7.11642 StartZ=0 EndX=7.28358 EndY=-6.975 EndZ=0
    g89: LineSegment StartX=7.06642 StartY=-7.475 StartZ=0 EndX=6.925 EndY=-7.33358 EndZ=0
    g90: LineSegment StartX=6.775 StartY=-7.76642 StartZ=0 EndX=6.63358 EndY=-7.625 EndZ=0
    g91: LineSegment StartX=6.41642 StartY=-8.125 StartZ=0 EndX=6.275 EndY=-7.98358 EndZ=0
    g92: LineSegment StartX=7.71642 StartY=-8.125 StartZ=0 EndX=7.575 EndY=-7.98358 EndZ=0
    g93: LineSegment StartX=7.425 StartY=-8.41642 StartZ=0 EndX=7.28358 EndY=-8.275 EndZ=0
    g94: LineSegment StartX=7.06642 StartY=-8.775 StartZ=0 EndX=6.925 EndY=-8.63358 EndZ=0
    g95: LineSegment StartX=6.775 StartY=-9.06642 StartZ=0 EndX=6.63358 EndY=-8.925 EndZ=0
    g96: LineSegment StartX=6.41642 StartY=-9.425 StartZ=0 EndX=6.275 EndY=-9.28358 EndZ=0
    g97: LineSegment StartX=7.425 StartY=-9.71642 StartZ=0 EndX=7.28358 EndY=-9.575 EndZ=0
    g98: LineSegment StartX=8.725 StartY=-9.71642 StartZ=0 EndX=8.58358 EndY=-9.575 EndZ=0
    g99: LineSegment StartX=8.075 StartY=-9.06642 StartZ=0 EndX=7.93358 EndY=-8.925 EndZ=0
    g100: LineSegment StartX=7.71642 StartY=-9.425 StartZ=0 EndX=7.575 EndY=-9.28358 EndZ=0
    g101: LineSegment StartX=9.01642 StartY=-9.425 StartZ=0 EndX=8.875 EndY=-9.28358 EndZ=0
    g102: LineSegment StartX=9.375 StartY=-9.06642 StartZ=0 EndX=9.23358 EndY=-8.925 EndZ=0
    g103: LineSegment StartX=8.725 StartY=-8.41642 StartZ=0 EndX=8.58358 EndY=-8.275 EndZ=0
    g104: LineSegment StartX=8.36642 StartY=-8.775 StartZ=0 EndX=8.225 EndY=-8.63358 EndZ=0
    g105: LineSegment StartX=9.66642 StartY=-8.775 StartZ=0 EndX=9.525 EndY=-8.63358 EndZ=0
    g106: LineSegment StartX=10.025 StartY=-8.41642 StartZ=0 EndX=9.88358 EndY=-8.275 EndZ=0
    g107: LineSegment StartX=10.675 StartY=-9.06642 StartZ=0 EndX=10.5336 EndY=-8.925 EndZ=0
    g108: LineSegment StartX=10.3164 StartY=-9.425 StartZ=0 EndX=10.175 EndY=-9.28358 EndZ=0
    g109: LineSegment StartX=10.025 StartY=-9.71642 StartZ=0 EndX=9.88358 EndY=-9.575 EndZ=0
    g110: LineSegment StartX=9.84142 StartY=-9.9 StartZ=0 EndX=9.55858 EndY=-9.9 EndZ=0
    g111: LineSegment StartX=8.54142 StartY=-9.9 StartZ=0 EndX=8.25858 EndY=-9.9 EndZ=0
    g112: LineSegment StartX=7.24142 StartY=-9.9 StartZ=0 EndX=6.95858 EndY=-9.9 EndZ=0
    g113: LineSegment StartX=11.1414 StartY=-9.9 StartZ=0 EndX=11.325 EndY=-9.71642 EndZ=0
    g114: LineSegment StartX=11.325 StartY=-9.71642 StartZ=0 EndX=11.1836 EndY=-9.575 EndZ=0
    g115: LineSegment StartX=11.1836 StartY=-9.575 StartZ=0 EndX=10.8586 EndY=-9.9 EndZ=0
    g116: LineSegment StartX=10.8586 StartY=-9.9 StartZ=0 EndX=11.1414 EndY=-9.9 EndZ=0
    g117: LineSegment [constr] StartX=11.4 StartY=-17.1 StartZ=0 EndX=8.4 EndY=-20.1 EndZ=0
    g118: LineSegment [constr] StartX=10.1 StartY=-17.1 StartZ=0 EndX=8.4 EndY=-18.8 EndZ=0
    g119: LineSegment [constr] StartX=8.8 StartY=-17.1 StartZ=0 EndX=8.4 EndY=-17.5 EndZ=0
    g120: LineSegment [constr] StartX=11.4 StartY=-18.4 StartZ=0 EndX=9.7 EndY=-20.1 EndZ=0
    g121: LineSegment [constr] StartX=11.4 StartY=-19.7 StartZ=0 EndX=11 EndY=-20.1 EndZ=0
    g122: LineSegment [constr] StartX=10.1 StartY=-17.1 StartZ=0 EndX=11.4 EndY=-18.4 EndZ=0
    g123: LineSegment [constr] StartX=8.8 StartY=-17.1 StartZ=0 EndX=11.4 EndY=-19.7 EndZ=0
    g124: LineSegment [constr] StartX=8.4 StartY=-18 StartZ=0 EndX=10.5 EndY=-20.1 EndZ=0
    g125: LineSegment [constr] StartX=8.4 StartY=-19.3 StartZ=0 EndX=9.2 EndY=-20.1 EndZ=0
    g126: LineSegment [constr] StartX=10.1 StartY=-17.1 StartZ=0 EndX=10.1 EndY=-18.4 EndZ=0
    g127: LineSegment [constr] StartX=8.8 StartY=-17.1 StartZ=0 EndX=8.8 EndY=-18.4 EndZ=0
    g128: LineSegment StartX=8.95 StartY=-17.1 StartZ=0 EndX=11.4 EndY=-19.55 EndZ=0
    g129: LineSegment StartX=11.4 StartY=-19.85 StartZ=0 EndX=8.65 EndY=-17.1 EndZ=0
    g130: LineSegment StartX=8.95 StartY=-17.1 StartZ=0 EndX=8.65 EndY=-17.1 EndZ=0
    g131: LineSegment StartX=11.4 StartY=-19.55 StartZ=0 EndX=11.4 EndY=-19.85 EndZ=0
    g132: LineSegment StartX=9.95 StartY=-17.1 StartZ=0 EndX=11.4 EndY=-18.55 EndZ=0
    g133: LineSegment StartX=11.4 StartY=-18.25 StartZ=0 EndX=10.25 EndY=-17.1 EndZ=0
    g134: LineSegment StartX=10.25 StartY=-17.1 StartZ=0 EndX=9.95 EndY=-17.1 EndZ=0
    g135: LineSegment StartX=11.4 StartY=-18.25 StartZ=0 EndX=11.4 EndY=-18.55 EndZ=0
    g136: LineSegment StartX=8.4 StartY=-17.85 StartZ=0 EndX=10.65 EndY=-20.1 EndZ=0
    g137: LineSegment StartX=10.35 StartY=-20.1 StartZ=0 EndX=8.4 EndY=-18.15 EndZ=0
    g138: LineSegment StartX=8.4 StartY=-18.15 StartZ=0 EndX=8.4 EndY=-17.85 EndZ=0
    g139: LineSegment StartX=10.65 StartY=-20.1 StartZ=0 EndX=10.35 EndY=-20.1 EndZ=0
    g140: LineSegment StartX=8.4 StartY=-19.15 StartZ=0 EndX=9.35 EndY=-20.1 EndZ=0
    g141: LineSegment StartX=8.4 StartY=-19.45 StartZ=0 EndX=9.05 EndY=-20.1 EndZ=0
    g142: LineSegment StartX=9.35 StartY=-20.1 StartZ=0 EndX=9.05 EndY=-20.1 EndZ=0
    g143: LineSegment StartX=8.4 StartY=-19.15 StartZ=0 EndX=8.4 EndY=-19.45 EndZ=0
    g144: LineSegment StartX=9.23358 StartY=-17.825 StartZ=0 EndX=9.375 EndY=-17.9664 EndZ=0
    g145: LineSegment StartX=9.375 StartY=-17.9664 StartZ=0 EndX=9.01642 EndY=-18.325 EndZ=0
    g146: LineSegment StartX=9.01642 StartY=-18.325 StartZ=0 EndX=8.875 EndY=-18.1836 EndZ=0
    g147: LineSegment StartX=8.875 StartY=-18.1836 StartZ=0 EndX=9.23358 EndY=-17.825 EndZ=0
    g148: LineSegment StartX=9.88358 StartY=-17.175 StartZ=0 EndX=10.025 EndY=-17.3164 EndZ=0
    g149: LineSegment StartX=10.025 StartY=-17.3164 StartZ=0 EndX=9.66642 EndY=-17.675 EndZ=0
    g150: LineSegment StartX=9.66642 StartY=-17.675 StartZ=0 EndX=9.525 EndY=-17.5336 EndZ=0
    g151: LineSegment StartX=9.525 StartY=-17.5336 StartZ=0 EndX=9.88358 EndY=-17.175 EndZ=0
    g152: LineSegment StartX=8.58358 StartY=-18.475 StartZ=0 EndX=8.725 EndY=-18.6164 EndZ=0
    g153: LineSegment StartX=8.725 StartY=-18.6164 StartZ=0 EndX=8.4 EndY=-18.9414 EndZ=0
    g154: LineSegment StartX=8.4 StartY=-18.9414 StartZ=0 EndX=8.4 EndY=-18.6586 EndZ=0
    g155: LineSegment StartX=8.58358 StartY=-18.475 StartZ=0 EndX=8.4 EndY=-18.6586 EndZ=0
    g156: LineSegment StartX=11.1856 StartY=-17.173 StartZ=0 EndX=10.825 EndY=-17.5336 EndZ=0
    g157: LineSegment StartX=10.825 StartY=-17.5336 StartZ=0 EndX=10.9664 EndY=-17.675 EndZ=0
    g158: LineSegment StartX=10.9664 StartY=-17.675 StartZ=0 EndX=11.327 EndY=-17.3144 EndZ=0
    g159: LineSegment StartX=11.327 StartY=-17.3144 StartZ=0 EndX=11.1856 EndY=-17.173 EndZ=0
    g160: LineSegment StartX=10.5336 StartY=-17.825 StartZ=0 EndX=10.675 EndY=-17.9664 EndZ=0
    g161: LineSegment StartX=10.675 StartY=-17.9664 StartZ=0 EndX=10.3164 EndY=-18.325 EndZ=0
    g162: LineSegment StartX=10.3164 StartY=-18.325 StartZ=0 EndX=10.175 EndY=-18.1836 EndZ=0
    g163: LineSegment StartX=10.5336 StartY=-17.825 StartZ=0 EndX=10.175 EndY=-18.1836 EndZ=0
    g164: LineSegment StartX=11.1836 StartY=-18.475 StartZ=0 EndX=11.325 EndY=-18.6164 EndZ=0
    g165: LineSegment StartX=11.325 StartY=-18.6164 StartZ=0 EndX=10.9664 EndY=-18.975 EndZ=0
    g166: LineSegment StartX=10.9664 StartY=-18.975 StartZ=0 EndX=10.825 EndY=-18.8336 EndZ=0
    g167: LineSegment StartX=11.1836 StartY=-18.475 StartZ=0 EndX=10.825 EndY=-18.8336 EndZ=0
    g168: LineSegment StartX=9.88358 StartY=-18.475 StartZ=0 EndX=10.025 EndY=-18.6164 EndZ=0
    g169: LineSegment StartX=10.025 StartY=-18.6164 StartZ=0 EndX=9.66642 EndY=-18.975 EndZ=0
    g170: LineSegment StartX=9.66642 StartY=-18.975 StartZ=0 EndX=9.525 EndY=-18.8336 EndZ=0
    g171: LineSegment StartX=9.88358 StartY=-18.475 StartZ=0 EndX=9.525 EndY=-18.8336 EndZ=0
    g172: LineSegment StartX=10.5336 StartY=-19.125 StartZ=0 EndX=10.675 EndY=-19.2664 EndZ=0
    g173: LineSegment StartX=10.675 StartY=-19.2664 StartZ=0 EndX=10.3164 EndY=-19.625 EndZ=0
    g174: LineSegment StartX=10.3164 StartY=-19.625 StartZ=0 EndX=10.175 EndY=-19.4836 EndZ=0
    g175: LineSegment StartX=10.5336 StartY=-19.125 StartZ=0 EndX=10.175 EndY=-19.4836 EndZ=0
    g176: LineSegment StartX=11.325 StartY=-19.9164 StartZ=0 EndX=11.1836 EndY=-19.775 EndZ=0
    g177: LineSegment StartX=11.1836 StartY=-19.775 StartZ=0 EndX=10.8586 EndY=-20.1 EndZ=0
    g178: LineSegment StartX=10.8586 StartY=-20.1 StartZ=0 EndX=11.1414 EndY=-20.1 EndZ=0
    g179: LineSegment StartX=11.325 StartY=-19.9164 StartZ=0 EndX=11.1414 EndY=-20.1 EndZ=0
    g180: LineSegment StartX=9.84142 StartY=-20.1 StartZ=0 EndX=10.025 EndY=-19.9164 EndZ=0
    g181: LineSegment StartX=10.025 StartY=-19.9164 StartZ=0 EndX=9.88358 EndY=-19.775 EndZ=0
    g182: LineSegment StartX=9.88358 StartY=-19.775 StartZ=0 EndX=9.55858 EndY=-20.1 EndZ=0
    g183: LineSegment StartX=9.55858 StartY=-20.1 StartZ=0 EndX=9.84142 EndY=-20.1 EndZ=0
    g184: LineSegment StartX=8.725 StartY=-19.9164 StartZ=0 EndX=8.58358 EndY=-19.775 EndZ=0
    g185: LineSegment StartX=8.58358 StartY=-19.775 StartZ=0 EndX=8.4 EndY=-19.9586 EndZ=0
    g186: LineSegment StartX=8.4 StartY=-19.9586 StartZ=0 EndX=8.4 EndY=-20.1 EndZ=0
    g187: LineSegment StartX=8.4 StartY=-20.1 StartZ=0 EndX=8.54142 EndY=-20.1 EndZ=0
    g188: LineSegment StartX=8.54142 StartY=-20.1 StartZ=0 EndX=8.725 EndY=-19.9164 EndZ=0
    g189: LineSegment StartX=9.375 StartY=-19.2664 StartZ=0 EndX=9.23358 EndY=-19.125 EndZ=0
    g190: LineSegment StartX=9.23358 StartY=-19.125 StartZ=0 EndX=8.875 EndY=-19.4836 EndZ=0
    g191: LineSegment StartX=8.875 StartY=-19.4836 StartZ=0 EndX=9.01642 EndY=-19.625 EndZ=0
    g192: LineSegment StartX=9.01642 StartY=-19.625 StartZ=0 EndX=9.375 EndY=-19.2664 EndZ=0
    g193: LineSegment StartX=8.58358 StartY=-17.175 StartZ=0 EndX=8.4 EndY=-17.3586 EndZ=0
    g194: LineSegment StartX=8.58358 StartY=-17.175 StartZ=0 EndX=8.725 EndY=-17.3164 EndZ=0
    g195: LineSegment StartX=8.725 StartY=-17.3164 StartZ=0 EndX=8.4 EndY=-17.6414 EndZ=0
    g196: LineSegment StartX=8.4 StartY=-17.6414 StartZ=0 EndX=8.4 EndY=-17.3586 EndZ=0
  constraints (603):
    c: DistanceY(g-8,g-8) = 3
    c: DistanceY(g-4,g-4) = 3
    c: DistanceX(g-12,g-11) = 0.7
    c: Coincident(g0,g-4)
    c: PointOnObject(g0,g-5)
    c: Angle(g0,g-4) = 0.785398
    c: PointOnObject(g1,g-5)
    c: PointOnObject(g1,g-13)
    c: Parallel(g1,g0)
    c: PointOnObject(g2,g-6)
    c: PointOnObject(g3,g-6)
    c: PointOnObject(g3,g-13)
    c: PointOnObject(g2,g-13)
    c: Parallel(g1,g2)
    c: Parallel(g0,g3)
    c: PointOnObject(g4,g-4)
    c: PointOnObject(g4,g-5)
    c: PointOnObject(g5,g-4)
    c: PointOnObject(g5,g-5)
    c: Parallel(g0,g4)
    c: Parallel(g4,g5)
    c: DistanceX(g3,g2) = 1.3
    c: DistanceX(g2,g1) = 1.3
    c: DistanceX(g1,g0) = 1.3
    c: DistanceY(g4,g0) = 1.3
    c: DistanceX(g-6,g3) = 1.3
    c: DistanceY(g5,g4) = 1.3
    c: Coincident(g6,g-6)
    c: PointOnObject(g6,g-5)
    c: Angle(g6,g-13) = 0.785398
    c: Coincident(g7,g3)
    c: PointOnObject(g7,g-5)
    c: Coincident(g8,g2)
    c: PointOnObject(g8,g-4)
    c: Coincident(g9,g1)
    c: PointOnObject(g9,g-4)
    c: Coincident(g10,g3)
    c: PointOnObject(g10,g-5)
    c: Coincident(g11,g2)
    c: PointOnObject(g11,g-5)
    c: Parallel(g6,g7)
    c: Parallel(g7,g8)
    c: Parallel(g8,g9)
    c: Parallel(g6,g10)
    c: Parallel(g10,g11)
    c: PointOnObject(g13,g-4)
    c: PointOnObject(g14,g-4)
    c: PointOnObject(g15,g-4)
    c: PointOnObject(g14,g-13)
    c: PointOnObject(g15,g-13)
    c: PointOnObject(g13,g-13)
    c: PointOnObject(g12,g-13)
    c: Parallel(g12,g8)
    c: PointOnObject(g12,g-4)
    c: Parallel(g8,g13)
    c: Parallel(g9,g15)
    c: Parallel(g9,g14)
    c: DistanceY(g5,g13) = 0.15
    c: DistanceY(g12,g5) = 0.15
    c: DistanceY(g15,g4) = 0.15
    c: DistanceY(g4,g14) = 0.15
    c: PointOnObject(g19,g-5)
    c: PointOnObject(g18,g-5)
    c: PointOnObject(g17,g-5)
    c: PointOnObject(g16,g-5)
    c: PointOnObject(g21,g-5)
    c: PointOnObject(g20,g-5)
    c: Parallel(g10,g21)
    c: Parallel(g10,g20)
    c: Parallel(g16,g7)
    c: Parallel(g17,g7)
    c: Parallel(g18,g6)
    c: Parallel(g19,g6)
    c: PointOnObject(g16,g-13)
    c: PointOnObject(g17,g-13)
    c: PointOnObject(g18,g-13)
    c: PointOnObject(g19,g-6)
    c: PointOnObject(g20,g-6)
    c: PointOnObject(g21,g-6)
    c: Parallel(g11,g22)
    c: PointOnObject(g22,g-6)
    c: PointOnObject(g22,g-5)
    c: Parallel(g23,g11)
    c: PointOnObject(g23,g-5)
    c: PointOnObject(g23,g-6)
    c: Coincident(g24,g14)
    c: Coincident(g24,g15)
    c: Coincident(g25,g13)
    c: Coincident(g25,g12)
    c: Coincident(g26,g16)
    c: Coincident(g26,g17)
    c: DistanceX(g3,g16) = 0.15
    c: DistanceX(g17,g3) = 0.15
    c: DistanceX(g6,g18) = 0.15
    c: DistanceY(g19,g6) = 0.15
    c: DistanceY(g3,g20) = 0.15
    c: DistanceY(g21,g3) = 0.15
    c: DistanceY(g2,g22) = 0.15
    c: DistanceY(g23,g2) = 0.15
    c: Coincident(g27,g18)
    c: Coincident(g27,g6)
    c: Coincident(g28,g6)
    c: Coincident(g28,g19)
    c: Coincident(g29,g20)
    c: Coincident(g29,g21)
    c: Coincident(g30,g22)
    c: Coincident(g30,g23)
    c: Coincident(g31,g23)
    c: Coincident(g31,g22)
    c: Coincident(g32,g21)
    c: Coincident(g32,g20)
    c: Coincident(g33,g19)
    c: Coincident(g33,g18)
    c: Coincident(g34,g17)
    c: Coincident(g34,g16)
    c: Coincident(g35,g12)
    c: Coincident(g35,g13)
    c: Coincident(g36,g15)
    c: Coincident(g36,g14)
    c: Coincident(g75,g74)
    c: Coincident(g75,g73)
    c: Coincident(g76,g74)
    c: Coincident(g76,g73)
    c: Coincident(g77,g42)
    c: Coincident(g77,g41)
    c: Coincident(g78,g42)
    c: Coincident(g78,g41)
    c: Coincident(g79,g40)
    c: Coincident(g79,g39)
    c: Coincident(g80,g40)
    c: Coincident(g80,g39)
    c: Coincident(g81,g44)
    c: Coincident(g81,g43)
    c: Coincident(g82,g44)
    c: Coincident(g82,g43)
    c: Coincident(g83,g46)
    c: Coincident(g83,g45)
    c: Coincident(g84,g46)
    c: Coincident(g84,g45)
    c: Coincident(g85,g64)
    c: Coincident(g85,g63)
    c: Coincident(g86,g64)
    c: Coincident(g86,g63)
    c: Coincident(g87,g62)
    c: Coincident(g87,g61)
    c: Coincident(g88,g66)
    c: Coincident(g88,g65)
    c: Coincident(g89,g66)
    c: Coincident(g89,g65)
    c: Coincident(g90,g68)
    c: Coincident(g90,g67)
    c: Coincident(g91,g68)
    c: Coincident(g91,g67)
    c: Coincident(g92,g62)
    c: Coincident(g92,g61)
    c: Coincident(g93,g60)
    c: Coincident(g93,g59)
    c: Coincident(g94,g60)
    c: Coincident(g94,g59)
    c: Coincident(g95,g58)
    c: Coincident(g95,g57)
    c: Coincident(g96,g58)
    c: Coincident(g96,g57)
    c: Coincident(g97,g56)
    c: Coincident(g97,g55)
    c: Coincident(g98,g54)
    c: Coincident(g98,g53)
    c: Coincident(g99,g70)
    c: Coincident(g99,g69)
    c: Coincident(g100,g70)
    c: Coincident(g100,g69)
    c: Coincident(g101,g50)
    c: Coincident(g101,g49)
    c: Coincident(g102,g50)
    c: Coincident(g102,g49)
    c: Coincident(g103,g48)
    c: Coincident(g103,g47)
    c: Coincident(g104,g48)
    c: Coincident(g104,g47)
    c: Coincident(g105,g38)
    c: Coincident(g105,g37)
    c: Coincident(g106,g38)
    c: Coincident(g106,g37)
    c: Coincident(g107,g72)
    c: Coincident(g107,g71)
    c: Coincident(g108,g72)
    c: Coincident(g108,g71)
    c: Coincident(g109,g52)
    c: Coincident(g109,g51)
    c: PointOnObject(g52,g-5)
    c: PointOnObject(g51,g-5)
    c: PointOnObject(g54,g-5)
    c: PointOnObject(g53,g-5)
    c: PointOnObject(g56,g-5)
    c: PointOnObject(g55,g-5)
    c: Coincident(g110,g52)
    c: Coincident(g110,g51)
    c: Coincident(g111,g54)
    c: Coincident(g111,g53)
    c: Coincident(g112,g56)
    c: Coincident(g112,g55)
    c: PointOnObject(g113,g-5)
    c: Coincident(g114,g113)
    c: Coincident(g115,g114)
    c: PointOnObject(g115,g-5)
    c: Coincident(g116,g115)
    c: Coincident(g116,g113)
    c: Parallel(g38,g0)
    c: Parallel(g37,g0)
    c: Parallel(g46,g1)
    c: Parallel(g45,g1)
    c: Parallel(g64,g2)
    c: Parallel(g63,g2)
    c: Parallel(g44,g1)
    c: Parallel(g43,g1)
    c: Parallel(g39,g0)
    c: Parallel(g40,g0)
    c: Parallel(g73,g4)
    c: Parallel(g74,g4)
    c: Parallel(g42,g0)
    c: Parallel(g41,g0)
    c: Parallel(g113,g5)
    c: Parallel(g115,g5)
    c: Parallel(g52,g4)
    c: Parallel(g51,g4)
    c: Parallel(g54,g0)
    c: Parallel(g53,g0)
    c: Parallel(g56,g1)
    c: Parallel(g55,g1)
    c: Parallel(g58,g2)
    c: Parallel(g57,g2)
    c: Parallel(g70,g1)
    c: Parallel(g69,g1)
    c: Parallel(g60,g2)
    c: Parallel(g59,g2)
    c: Parallel(g68,g3)
    c: Parallel(g67,g3)
    c: Parallel(g66,g3)
    c: Parallel(g65,g3)
    c: Parallel(g61,g2)
    c: Parallel(g62,g2)
    c: Parallel(g48,g1)
    c: Parallel(g47,g1)
    c: Parallel(g49,g0)
    c: Parallel(g50,g0)
    c: Parallel(g72,g4)
    c: Parallel(g71,g4)
    c: Parallel(g81,g15)
    c: Parallel(g79,g15)
    c: Parallel(g76,g15)
    c: Parallel(g78,g14)
    c: Parallel(g77,g14)
    c: Parallel(g82,g13)
    c: Parallel(g80,g13)
    c: Parallel(g75,g13)
    c: Parallel(g114,g12)
    c: Parallel(g107,g12)
    c: Parallel(g12,g106)
    c: Parallel(g83,g12)
    c: Parallel(g86,g12)
    c: Parallel(g85,g16)
    c: Parallel(g84,g16)
    c: Parallel(g105,g16)
    c: Parallel(g108,g16)
    c: Parallel(g109,g17)
    c: Parallel(g102,g17)
    c: Parallel(g101,g18)
    c: Parallel(g103,g17)
    c: Parallel(g104,g18)
    c: Parallel(g87,g17)
    c: Parallel(g92,g18)
    c: Parallel(g88,g17)
    c: Parallel(g89,g18)
    c: Parallel(g90,g19)
    c: Parallel(g93,g19)
    c: Parallel(g99,g19)
    c: Parallel(g98,g19)
    c: Parallel(g97,g21)
    c: Parallel(g95,g21)
    c: Parallel(g96,g22)
    c: Distance(g57,g2) = 0.1
    c: Distance(g58,g2) = 0.1
    c: Distance(g57,g21) = 0.1
    c: Distance(g57,g22) = 0.1
    c: Distance(g59,g2) = 0.1
    c: Distance(g60,g2) = 0.1
    c: Parallel(g94,g20)
    c: Distance(g59,g20) = 0.1
    c: Distance(g59,g19) = 0.1
    c: Distance(g69,g1) = 0.1
    c: Distance(g70,g1) = 0.1
    c: Parallel(g100,g20)
    c: Distance(g56,g1) = 0.1
    c: Distance(g55,g1) = 0.1
    c: Distance(g54,g0) = 0.1
    c: Distance(g53,g0) = 0.1
    c: Distance(g50,g0) = 0.1
    c: Distance(g49,g0) = 0.1
    c: Distance(g48,g1) = 0.1
    c: Distance(g47,g1) = 0.1
    c: Distance(g56,g21) = 0.1
    c: Distance(g54,g19) = 0.1
    c: Distance(g70,g19) = 0.1
    c: Distance(g70,g20) = 0.1
    c: Parallel(g91,g20)
    c: Distance(g68,g3) = 0.1
    c: Distance(g67,g3) = 0.1
    c: Distance(g68,g19) = 0.1
    c: Distance(g68,g20) = 0.1
    c: Distance(g52,g4) = 0.1
    c: Distance(g51,g4) = 0.1
    c: Distance(g52,g17) = 0.1
    c: Distance(g50,g17) = 0.1
    c: Distance(g50,g18) = 0.1
    c: Distance(g47,g18) = 0.1
    c: Distance(g48,g17) = 0.1
    c: Distance(g62,g2) = 0.1
    c: Distance(g61,g2) = 0.1
    c: Distance(g62,g17) = 0.1
    c: Distance(g62,g18) = 0.1
    c: Distance(g66,g3) = 0.1
    c: Distance(g65,g3) = 0.1
    c: Distance(g66,g18) = 0.1
    c: Distance(g66,g17) = 0.1
    c: Distance(g64,g2) = 0.1
    c: Distance(g63,g2) = 0.1
    c: Distance(g64,g16) = 0.1
    c: Distance(g64,g12) = 0.1
    c: Distance(g46,g1) = 0.1
    c: Distance(g45,g1) = 0.1
    c: Distance(g46,g12) = 0.1
    c: Distance(g46,g16) = 0.1
    c: Distance(g37,g0) = 0.1
    c: Distance(g38,g0) = 0.1
    c: Distance(g38,g12) = 0.1
    c: Distance(g38,g16) = 0.1
    c: Distance(g72,g4) = 0.1
    c: Distance(g71,g4) = 0.1
    c: Distance(g72,g12) = 0.1
    c: Distance(g72,g16) = 0.1
    c: Distance(g113,g5) = 0.1
    c: Distance(g114,g5) = 0.1
    c: Distance(g113,g12) = 0.1
    c: Distance(g74,g4) = 0.1
    c: Distance(g73,g4) = 0.1
    c: Distance(g74,g13) = 0.1
    c: Distance(g74,g15) = 0.1
    c: Distance(g40,g0) = 0.1
    c: Distance(g39,g0) = 0.1
    c: Distance(g40,g13) = 0.1
    c: Distance(g40,g15) = 0.1
    c: Distance(g44,g1) = 0.1
    c: Distance(g43,g1) = 0.1
    c: Distance(g44,g13) = 0.1
    c: Distance(g44,g15) = 0.1
    c: Distance(g42,g0) = 0.1
    c: Distance(g41,g0) = 0.1
    c: Distance(g42,g14) = 0.1
    c: Distance(g41) = 0.51
    c: Coincident(g117,g-8)
    c: Coincident(g117,g-10)
    c: PointOnObject(g118,g-7)
    c: PointOnObject(g119,g-7)
    c: DistanceX(g118,g117) = 1.3
    c: DistanceX(g119,g118) = 1.3
    c: Angle(g-7,g118) = 0.785398
    c: Angle(g119,g-7) = 2.35619
    c: PointOnObject(g119,g-9)
    c: PointOnObject(g118,g-9)
    c: PointOnObject(g120,g-8)
    c: PointOnObject(g121,g-8)
    c: PointOnObject(g120,g-10)
    c: PointOnObject(g121,g-10)
    c: Angle(g120,g-8) = 0.785398
    c: Angle(g-8,g121) = 2.35619
    c: DistanceY(g120,g117) = 1.3
    c: DistanceY(g121,g120) = 1.3
    c: Coincident(g122,g118)
    c: Coincident(g123,g119)
    c: Angle(g123,g-7) = 0.785398
    c: Angle(g-7,g122) = 2.35619
    c: PointOnObject(g122,g-8)
    c: PointOnObject(g123,g-8)
    c: PointOnObject(g124,g-9)
    c: PointOnObject(g125,g-9)
    c: Angle(g-9,g124) = 0.785398
    c: Angle(g125,g-9) = 2.35619
    c: PointOnObject(g125,g-10)
    c: PointOnObject(g124,g-10)
    c: DistanceY(g125,g124) = 1.3
    c: Coincident(g126,g118)
    c: PointOnObject(g126,g117)
    c: Vertical(g126)
    c: Coincident(g127,g119)
    c: PointOnObject(g127,g118)
    c: Vertical(g127)
    c: PointOnObject(g127,g124)
    c: PointOnObject(g128,g-7)
    c: PointOnObject(g128,g-8)
    c: PointOnObject(g129,g-8)
    c: PointOnObject(g129,g-7)
    c: Coincident(g130,g128)
    c: Coincident(g130,g129)
    c: Coincident(g131,g128)
    c: Coincident(g131,g129)
    c: DistanceY(g121,g128) = 0.15
    c: DistanceY(g129,g121) = 0.15
    c: Parallel(g128,g123)
    c: Parallel(g129,g123)
    c: PointOnObject(g132,g-7)
    c: PointOnObject(g132,g-8)
    c: PointOnObject(g133,g-8)
    c: PointOnObject(g133,g-7)
    c: Coincident(g134,g133)
    c: Coincident(g134,g132)
    c: Coincident(g135,g133)
    c: Coincident(g135,g132)
    c: Parallel(g122,g132)
    c: Parallel(g122,g133)
    c: DistanceY(g120,g133) = 0.15
    c: DistanceY(g132,g120) = 0.15
    c: PointOnObject(g136,g-9)
    c: PointOnObject(g136,g-10)
    c: PointOnObject(g137,g-10)
    c: PointOnObject(g137,g-9)
    c: Coincident(g138,g137)
    c: Coincident(g138,g136)
    c: Coincident(g139,g136)
    c: Coincident(g139,g137)
    c: Parallel(g136,g124)
    c: Parallel(g137,g124)
    c: DistanceY(g124,g136) = 0.15
    c: DistanceY(g137,g124) = 0.15
    c: PointOnObject(g140,g-9)
    c: PointOnObject(g140,g-10)
    c: PointOnObject(g141,g-9)
    c: PointOnObject(g141,g-10)
    c: Coincident(g142,g140)
    c: Coincident(g142,g141)
    c: Coincident(g143,g140)
    c: Coincident(g143,g141)
    c: DistanceX(g125,g140) = 0.15
    c: DistanceX(g141,g125) = 0.15
    c: Parallel(g125,g141)
    c: Parallel(g125,g140)
    c: Coincident(g145,g144)
    c: Coincident(g146,g145)
    c: Coincident(g147,g146)
    c: Coincident(g147,g144)
    c: Coincident(g149,g148)
    c: Coincident(g150,g149)
    c: Coincident(g151,g150)
    c: Coincident(g151,g148)
    c: Coincident(g153,g152)
    c: PointOnObject(g153,g-9)
    c: Coincident(g154,g153)
    c: PointOnObject(g154,g-9)
    c: Coincident(g155,g152)
    c: Coincident(g155,g154)
    c: Coincident(g157,g156)
    c: Coincident(g158,g157)
    c: Coincident(g159,g158)
    c: Coincident(g159,g156)
    c: Coincident(g161,g160)
    c: Coincident(g162,g161)
    c: Coincident(g163,g160)
    c: Coincident(g163,g162)
    c: Coincident(g165,g164)
    c: Coincident(g166,g165)
    c: Coincident(g167,g164)
    c: Coincident(g167,g166)
    c: Coincident(g169,g168)
    c: Coincident(g170,g169)
    c: Coincident(g171,g168)
    c: Coincident(g171,g170)
    c: Coincident(g173,g172)
    c: Coincident(g174,g173)
    c: Coincident(g175,g172)
    c: Coincident(g175,g174)
    c: Coincident(g177,g176)
    c: PointOnObject(g177,g-10)
    c: Coincident(g178,g177)
    c: PointOnObject(g178,g-10)
    c: Coincident(g179,g176)
    c: Coincident(g179,g178)
    c: PointOnObject(g180,g-10)
    c: Coincident(g181,g180)
    c: Coincident(g182,g181)
    c: PointOnObject(g182,g-10)
    c: Coincident(g183,g182)
    c: Coincident(g183,g180)
    c: Coincident(g185,g184)
    c: PointOnObject(g185,g-9)
    c: Coincident(g186,g185)
    c: Coincident(g186,g117)
    c: Coincident(g187,g117)
    c: PointOnObject(g187,g-10)
    c: Coincident(g188,g187)
    c: Coincident(g188,g184)
    c: Coincident(g190,g189)
    c: Coincident(g191,g190)
    c: Coincident(g192,g191)
    c: Coincident(g192,g189)
    c: Parallel(g190,g117)
    c: Parallel(g192,g117)
    c: Parallel(g188,g117)
    c: Parallel(g185,g117)
    c: Parallel(g182,g120)
    c: Parallel(g180,g120)
    c: Parallel(g173,g120)
    c: Parallel(g175,g120)
    c: Parallel(g179,g121)
    c: Parallel(g177,g121)
    c: Parallel(g165,g120)
    c: Parallel(g167,g120)
    c: Parallel(g158,g117)
    c: Parallel(g156,g117)
    c: Parallel(g161,g117)
    c: Parallel(g163,g117)
    c: Parallel(g149,g118)
    c: Parallel(g151,g118)
    c: PointOnObject(g193,g-9)
    c: Coincident(g194,g193)
    c: Coincident(g195,g194)
    c: PointOnObject(g195,g-9)
    c: Coincident(g196,g195)
    c: Coincident(g196,g193)
    c: Parallel(g193,g119)
    c: Parallel(g195,g119)
    c: Perpendicular(g194,g195)
    c: Perpendicular(g147,g144)
    c: Perpendicular(g146,g145)
    c: Perpendicular(g150,g149)
    c: Perpendicular(g149,g148)
    c: Perpendicular(g160,g163)
    c: Perpendicular(g162,g161)
    c: Perpendicular(g157,g158)
    c: Perpendicular(g158,g159)
    c: Perpendicular(g167,g164)
    c: Perpendicular(g166,g165)
    c: Perpendicular(g174,g173)
    c: Perpendicular(g175,g172)
    c: Perpendicular(g176,g179)
    c: Perpendicular(g181,g180)
    c: Perpendicular(g184,g188)
    c: Perpendicular(g191,g192)
    c: Perpendicular(g189,g192)
    c: Perpendicular(g170,g169)
    c: Perpendicular(g171,g168)
    c: Parallel(g171,g117)
    c: Parallel(g169,g117)
    c: Parallel(g155,g118)
    c: Parallel(g153,g118)
    c: Distance(g150,g118) = 0.1
    c: Distance(g149,g118) = 0.1
    c: Distance(g149,g128) = 0.1
    c: Distance(g148,g132) = 0.1
    c: Distance(g160,g117) = 0.1
    c: Distance(g160,g117) = 0.1
    c: Distance(g160,g132) = 0.1
    c: Distance(g161,g128) = 0.1
    c: Distance(g164,g120) = 0.1
    c: Distance(g164,g120) = 0.1
    c: Distance(g164,g132) = 0.1
    c: Distance(g166,g128) = 0.1
    c: Distance(g156,g117) = 0.1
    c: Distance(g158,g117) = 0.1
    c: Distance(g156,g133) = 0.1
    c: Distance(g156) = 0.51
    c: Distance(g194,g119) = 0.1
    c: Distance(g193,g119) = 0.1
    c: Distance(g194,g129) = 0.1
    c: Distance(g144,g118) = 0.1
    c: Distance(g144,g118) = 0.1
    c: Distance(g144,g129) = 0.1
    c: Parallel(g145,g118)
    c: Parallel(g147,g118)
    c: Distance(g146,g136) = 0.1
    c: Distance(g168,g117) = 0.1
    c: Distance(g168,g117) = 0.1
    c: Distance(g168,g129) = 0.1
    c: Distance(g170,g136) = 0.1
    c: Distance(g172,g120) = 0.1
    c: Distance(g172,g120) = 0.1
    c: Distance(g172,g129) = 0.1
    c: Distance(g174,g136) = 0.1
    c: Distance(g176,g121) = 0.1
    c: Distance(g176,g121) = 0.1
    c: Distance(g176,g129) = 0.1
    c: Distance(g152,g118) = 0.1
    c: Distance(g152,g118) = 0.1
    c: Distance(g152,g137) = 0.1
    c: Parallel(g152,g124)
    c: Distance(g189,g117) = 0.1
    c: Distance(g189,g117) = 0.1
    c: Distance(g189,g137) = 0.1
    c: Distance(g191,g140) = 0.1
    c: Distance(g180,g120) = 0.1
    c: Distance(g181,g120) = 0.1
    c: Distance(g181,g137) = 0.1
    c: Distance(g184,g117) = 0.1
    c: Distance(g184,g117) = 0.1
    c: Distance(g184,g141) = 0.1
FEATURE [PartDesign::Pad] Pad009
  BaseFeature = -> Pad008
  Direction = (0,0,1)
  Length = 0.2
  Length2 = 10
  Profile = -> Sketch009
  ReferenceAxis = -> Sketch009 [N_Axis]
  Refine = true
  Suppressed = false
  Type = 0
FEATURE [Sketcher::SketchObject] Sketch010
  ArcFitTolerance = 1e-06
  AttachmentSupport = -> [Pad009]
  ExternalGeometry = -> [Pad009]
  FullyConstrained = true
  MakeInternals = false
  MapMode = 5
  Placement = pos=(0,0,4.2) rot=(0,0,1;0rad)
  sketch-geometry (40):
    g0: LineSegment StartX=6.7 StartY=-6.9 StartZ=0 EndX=6.2 EndY=-7.4 EndZ=0
    g1: LineSegment StartX=6.2 StartY=-7.4 StartZ=0 EndX=6.2 EndY=-7.7 EndZ=0
    g2: LineSegment StartX=6.2 StartY=-7.7 StartZ=0 EndX=7 EndY=-6.9 EndZ=0
    g3: LineSegment StartX=7 StartY=-6.9 StartZ=0 EndX=6.7 EndY=-6.9 EndZ=0
    g4: LineSegment StartX=8 StartY=-6.9 StartZ=0 EndX=8.3 EndY=-6.9 EndZ=0
    g5: LineSegment StartX=8.3 StartY=-6.9 StartZ=0 EndX=6.2 EndY=-9 EndZ=0
    g6: LineSegment StartX=6.2 StartY=-9 StartZ=0 EndX=6.2 EndY=-8.7 EndZ=0
    g7: LineSegment StartX=6.2 StartY=-8.7 StartZ=0 EndX=8 EndY=-6.9 EndZ=0
    g8: LineSegment StartX=9.3 StartY=-6.9 StartZ=0 EndX=9.6 EndY=-6.9 EndZ=0
    g9: LineSegment StartX=9.6 StartY=-6.9 StartZ=0 EndX=6.6 EndY=-9.9 EndZ=0
    g10: LineSegment StartX=6.6 StartY=-9.9 StartZ=0 EndX=6.3 EndY=-9.9 EndZ=0
    g11: LineSegment StartX=6.3 StartY=-9.9 StartZ=0 EndX=9.3 EndY=-6.9 EndZ=0
    g12: LineSegment StartX=10.6 StartY=-6.9 StartZ=0 EndX=10.9 EndY=-6.9 EndZ=0
    g13: LineSegment StartX=10.9 StartY=-6.9 StartZ=0 EndX=7.9 EndY=-9.9 EndZ=0
    g14: LineSegment StartX=7.9 StartY=-9.9 StartZ=0 EndX=7.6 EndY=-9.9 EndZ=0
    g15: LineSegment StartX=7.6 StartY=-9.9 StartZ=0 EndX=10.6 EndY=-6.9 EndZ=0
    g16: LineSegment StartX=11.4 StartY=-7.4 StartZ=0 EndX=11.4 EndY=-7.7 EndZ=0
    g17: LineSegment StartX=11.4 StartY=-7.7 StartZ=0 EndX=9.2 EndY=-9.9 EndZ=0
    g18: LineSegment StartX=9.2 StartY=-9.9 StartZ=0 EndX=8.9 EndY=-9.9 EndZ=0
    g19: LineSegment StartX=8.9 StartY=-9.9 StartZ=0 EndX=11.4 EndY=-7.4 EndZ=0
    g20: LineSegment StartX=11.4 StartY=-8.7 StartZ=0 EndX=11.4 EndY=-9 EndZ=0
    g21: LineSegment StartX=11.4 StartY=-9 StartZ=0 EndX=10.5 EndY=-9.9 EndZ=0
    g22: LineSegment StartX=10.5 StartY=-9.9 StartZ=0 EndX=10.2 EndY=-9.9 EndZ=0
    g23: LineSegment StartX=10.2 StartY=-9.9 StartZ=0 EndX=11.4 EndY=-8.7 EndZ=0
    g24: LineSegment StartX=9.3 StartY=-17.1 StartZ=0 EndX=9.6 EndY=-17.1 EndZ=0
    g25: LineSegment StartX=9.6 StartY=-17.1 StartZ=0 EndX=8.4 EndY=-18.3 EndZ=0
    g26: LineSegment StartX=8.4 StartY=-18.3 StartZ=0 EndX=8.4 EndY=-18 EndZ=0
    g27: LineSegment StartX=8.4 StartY=-18 StartZ=0 EndX=9.3 EndY=-17.1 EndZ=0
    g28: LineSegment StartX=10.6 StartY=-17.1 StartZ=0 EndX=10.9 EndY=-17.1 EndZ=0
    g29: LineSegment StartX=10.9 StartY=-17.1 StartZ=0 EndX=8.4 EndY=-19.6 EndZ=0
    g30: LineSegment StartX=8.4 StartY=-19.6 StartZ=0 EndX=8.4 EndY=-19.3 EndZ=0
    g31: LineSegment StartX=8.4 StartY=-19.3 StartZ=0 EndX=10.6 EndY=-17.1 EndZ=0
    g32: LineSegment StartX=11.4 StartY=-17.6 StartZ=0 EndX=11.4 EndY=-17.9 EndZ=0
    g33: LineSegment StartX=11.4 StartY=-17.6 StartZ=0 EndX=8.9 EndY=-20.1 EndZ=0
    g34: LineSegment StartX=8.9 StartY=-20.1 StartZ=0 EndX=9.2 EndY=-20.1 EndZ=0
    g35: LineSegment StartX=9.2 StartY=-20.1 StartZ=0 EndX=11.4 EndY=-17.9 EndZ=0
    g36: LineSegment StartX=11.4 StartY=-18.9 StartZ=0 EndX=11.4 EndY=-19.2 EndZ=0
    g37: LineSegment StartX=11.4 StartY=-19.2 StartZ=0 EndX=10.5 EndY=-20.1 EndZ=0
    g38: LineSegment StartX=10.5 StartY=-20.1 StartZ=0 EndX=10.2 EndY=-20.1 EndZ=0
    g39: LineSegment StartX=10.2 StartY=-20.1 StartZ=0 EndX=11.4 EndY=-18.9 EndZ=0
  constraints (120):
    c: PointOnObject(g0,g-18)
    c: PointOnObject(g0,g-16)
    c: Coincident(g1,g0)
    c: PointOnObject(g1,g-16)
    c: Coincident(g2,g1)
    c: PointOnObject(g2,g-18)
    c: Coincident(g3,g2)
    c: Coincident(g3,g0)
    c: PointOnObject(g4,g-18)
    c: PointOnObject(g4,g-18)
    c: Coincident(g5,g4)
    c: PointOnObject(g5,g-16)
    c: Coincident(g6,g5)
    c: PointOnObject(g6,g-16)
    c: Coincident(g7,g6)
    c: Coincident(g7,g4)
    c: PointOnObject(g8,g-18)
    c: PointOnObject(g8,g-18)
    c: Coincident(g9,g8)
    c: PointOnObject(g9,g-17)
    c: Coincident(g10,g9)
    c: PointOnObject(g10,g-17)
    c: Coincident(g11,g10)
    c: Coincident(g11,g8)
    c: PointOnObject(g12,g-18)
    c: PointOnObject(g12,g-18)
    c: Coincident(g13,g12)
    c: PointOnObject(g13,g-17)
    c: Coincident(g14,g13)
    c: PointOnObject(g14,g-17)
    c: Coincident(g15,g14)
    c: Coincident(g15,g12)
    c: PointOnObject(g16,g-19)
    c: PointOnObject(g16,g-19)
    c: Coincident(g17,g16)
    c: PointOnObject(g17,g-17)
    c: Coincident(g18,g17)
    c: PointOnObject(g18,g-17)
    c: Coincident(g19,g18)
    c: Coincident(g19,g16)
    c: PointOnObject(g20,g-19)
    c: PointOnObject(g20,g-19)
    c: Coincident(g21,g20)
    c: PointOnObject(g21,g-17)
    c: Coincident(g22,g21)
    c: PointOnObject(g22,g-17)
    c: Coincident(g23,g20)
    c: Coincident(g22,g23)
    c: DistanceX(g0,g2) = 0.3
    c: DistanceX(g4,g4) = 0.3
    c: DistanceX(g8,g8) = 0.3
    c: DistanceX(g12,g12) = 0.3
    c: Parallel(g0,g-22)
    c: Parallel(g2,g-22)
    c: Parallel(g7,g-23)
    c: Parallel(g5,g-23)
    c: Parallel(g11,g-24)
    c: Parallel(g9,g-24)
    c: Parallel(g15,g-20)
    c: Parallel(g13,g-20)
    c: Parallel(g17,g-21)
    c: Parallel(g19,g-21)
    c: Parallel(g23,g-21)
    c: Parallel(g21,g-21)
    c: DistanceY(g20,g20) = 0.3
    c: DistanceY(g16,g16) = 0.3
    c: DistanceX(g-18,g0) = 0.5
    c: DistanceX(g2,g4) = 1
    c: DistanceX(g4,g8) = 1
    c: DistanceX(g8,g12) = 1
    c: DistanceX(g13,g18) = 1
    c: DistanceX(g17,g22) = 1
    c: PointOnObject(g24,g-31)
    c: PointOnObject(g24,g-31)
    c: Coincident(g25,g24)
    c: PointOnObject(g25,g-30)
    c: Coincident(g26,g25)
    c: PointOnObject(g26,g-30)
    c: Coincident(g27,g26)
    c: Coincident(g27,g24)
    c: PointOnObject(g28,g-31)
    c: PointOnObject(g28,g-31)
    c: Coincident(g29,g28)
    c: PointOnObject(g29,g-30)
    c: Coincident(g30,g29)
    c: PointOnObject(g30,g-30)
    c: Coincident(g31,g30)
    c: Coincident(g31,g28)
    c: PointOnObject(g32,g-28)
    c: PointOnObject(g32,g-28)
    c: Coincident(g33,g32)
    c: PointOnObject(g33,g-29)
    c: Coincident(g34,g33)
    c: PointOnObject(g34,g-29)
    c: Coincident(g35,g34)
    c: Coincident(g35,g32)
    c: PointOnObject(g36,g-28)
    c: PointOnObject(g36,g-28)
    c: Coincident(g37,g36)
    c: PointOnObject(g37,g-29)
    c: Coincident(g38,g37)
    c: PointOnObject(g38,g-29)
    c: Coincident(g39,g38)
    c: Coincident(g39,g36)
    c: DistanceX(g24,g24) = 0.3
    c: Parallel(g27,g25)
    c: Parallel(g31,g29)
    c: Parallel(g33,g35)
    c: Parallel(g39,g37)
    c: DistanceY(g36,g36) = 0.3
    c: DistanceY(g32,g32) = 0.3
    c: DistanceX(g28,g28) = 0.3
    c: DistanceX(g24,g28) = 1
    c: DistanceY(g36,g32) = 1
    c: Parallel(g29,g33)
    c: Parallel(g35,g39)
    c: Parallel(g31,g25)
    c: Parallel(g29,g-32)
    c: DistanceX(g-31,g24) = 0.9
    c: DistanceX(g37,g-29) = 0.9
FEATURE [PartDesign::Pocket] Pocket
  BaseFeature = -> Pad009
  Direction = (0,0,-1)
  Length = 0.2
  Length2 = 5
  Profile = -> Sketch010
  ReferenceAxis = -> Sketch010 [N_Axis]
  Refine = true
  Suppressed = false
  Type = 0
FEATURE [Sketcher::SketchObject] Sketch011
  ArcFitTolerance = 1e-06
  AttachmentSupport = -> [Pocket]
  ExternalGeometry = -> [Pocket]
  FullyConstrained = true
  MakeInternals = false
  MapMode = 5
  Placement = pos=(0,0,2) rot=(0,0,1;0rad)
  sketch-geometry (12):
    g0: LineSegment StartX=5.5 StartY=-23.7 StartZ=0 EndX=5.5 EndY=-30.8 EndZ=0
    g1: LineSegment StartX=6 StartY=-31.3 StartZ=0 EndX=17.2 EndY=-31.3 EndZ=0
    g2: LineSegment StartX=17.7 StartY=-30.8 StartZ=0 EndX=17.7 EndY=-23.7 EndZ=0
    g3: LineSegment StartX=17.2 StartY=-23.2 StartZ=0 EndX=6 EndY=-23.2 EndZ=0
    g4: ArcOfCircle CenterX=17.2 CenterY=-30.8 CenterZ=0 NormalX=0 NormalY=0 NormalZ=1 AngleXU=0 Radius=0.5 StartAngle=4.71239 EndAngle=6.28319
    g5: GeomPoint [constr] X=17.7 Y=-31.3 Z=0
    g6: ArcOfCircle CenterX=17.2 CenterY=-23.7 CenterZ=0 NormalX=0 NormalY=0 NormalZ=1 AngleXU=0 Radius=0.5 StartAngle=-1.8e-15 EndAngle=1.5708
    g7: GeomPoint [constr] X=17.7 Y=-23.2 Z=0
    g8: ArcOfCircle CenterX=6 CenterY=-23.7 CenterZ=0 NormalX=0 NormalY=0 NormalZ=1 AngleXU=0 Radius=0.5 StartAngle=1.5708 EndAngle=3.14159
    g9: GeomPoint [constr] X=5.5 Y=-23.2 Z=0
    g10: ArcOfCircle CenterX=6 CenterY=-30.8 CenterZ=0 NormalX=0 NormalY=0 NormalZ=1 AngleXU=0 Radius=0.5 StartAngle=3.14159 EndAngle=4.71239
    g11: GeomPoint [constr] X=5.5 Y=-31.3 Z=0
  constraints (28):
    c: Vertical(g0)
    c: Vertical(g2)
    c: Horizontal(g1)
    c: Horizontal(g3)
    c: PointOnObject(g5,g1)
    c: PointOnObject(g5,g2)
    c: Tangent(g1,g4) = -1.5708
    c: Tangent(g2,g4) = -1.5708
    c: PointOnObject(g7,g2)
    c: PointOnObject(g7,g3)
    c: Tangent(g2,g6) = -1.5708
    c: Tangent(g3,g6) = -1.5708
    c: PointOnObject(g9,g0)
    c: PointOnObject(g9,g3)
    c: Tangent(g0,g8) = -1.5708
    c: Tangent(g3,g8) = -1.5708
    c: PointOnObject(g11,g0)
    c: PointOnObject(g11,g1)
    c: Tangent(g0,g10) = -1.5708
    c: Tangent(g1,g10) = -1.5708
    c: Radius(g8) = 0.5
    c: Radius(g10) = 0.5
    c: Radius(g6) = 0.5
    c: Radius(g4) = 0.5
    c: DistanceX(g0,g2) = 12.2
    c: DistanceY(g1,g3) = 8.1
    c: DistanceY(g-3,g1) = 0.7
    c: DistanceX(g-3,g0) = 3
FEATURE [PartDesign::Pad] Pad010
  BaseFeature = -> Pocket
  Direction = (0,0,1)
  Length = 0.3
  Length2 = 10
  Profile = -> Sketch011
  ReferenceAxis = -> Sketch011 [N_Axis]
  Refine = true
  Suppressed = false
  Type = 0
FEATURE [Sketcher::SketchObject] Sketch012
  ArcFitTolerance = 1e-06
  AttachmentSupport = -> [Pad010]
  ExternalGeometry = -> [Pad010]
  FullyConstrained = true
  MakeInternals = false
  MapMode = 5
  Placement = pos=(0,0,2) rot=(0,0,1;0rad)
  sketch-geometry (8):
    g0: Circle CenterX=25.5 CenterY=-28.1 CenterZ=0 NormalX=0 NormalY=0 NormalZ=1 AngleXU=0 Radius=2.5
    g1: Circle CenterX=38.5 CenterY=-28.1 CenterZ=0 NormalX=0 NormalY=0 NormalZ=1 AngleXU=0 Radius=2.5
    g2: LineSegment [constr] StartX=25.5 StartY=-28.1 StartZ=0 EndX=25.5 EndY=-30.6 EndZ=0
    g3: LineSegment [constr] StartX=38.5 StartY=-28.1 StartZ=0 EndX=38.5 EndY=-30.6 EndZ=0
    g4: LineSegment [constr] StartX=38.5 StartY=-28.1 StartZ=0 EndX=41 EndY=-28.1 EndZ=0
    g5: LineSegment [constr] StartX=25.5 StartY=-28.1 StartZ=0 EndX=28 EndY=-28.1 EndZ=0
    g6: LineSegment [constr] StartX=38.5 StartY=-28.1 StartZ=0 EndX=36 EndY=-28.1 EndZ=0
    g7: LineSegment [constr] StartX=36 StartY=-28.1 StartZ=0 EndX=28 EndY=-28.1 EndZ=0
  constraints (23):
    c: Diameter(g0) = 5
    c: Diameter(g1) = 5
    c: Coincident(g2,g0)
    c: PointOnObject(g2,g0)
    c: Vertical(g2)
    c: Coincident(g3,g1)
    c: PointOnObject(g3,g1)
    c: Vertical(g3)
    c: Coincident(g4,g1)
    c: PointOnObject(g4,g1)
    c: Horizontal(g4)
    c: Coincident(g5,g0)
    c: PointOnObject(g5,g0)
    c: Horizontal(g5)
    c: DistanceX(g4,g-5) = 1.5
    c: Coincident(g6,g1)
    c: PointOnObject(g6,g1)
    c: Horizontal(g6)
    c: Coincident(g7,g6)
    c: Coincident(g7,g5)
    c: Horizontal(g7)
    c: DistanceX(g5,g6) = 8
    c: DistanceY(g-5,g3) = 1.4
FEATURE [PartDesign::Pad] Pad011
  BaseFeature = -> Pad010
  Direction = (0,0,1)
  Length = 0.3
  Length2 = 10
  Profile = -> Sketch012
  ReferenceAxis = -> Sketch012 [N_Axis]
  Refine = true
  Suppressed = false
  Type = 0
FEATURE [Sketcher::SketchObject] Sketch013
  ArcFitTolerance = 1e-06
  AttachmentSupport = -> [Pad011]
  ExternalGeometry = -> [Pad011]
  FullyConstrained = true
  MakeInternals = false
  MapMode = 5
  Placement = pos=(0,0,2) rot=(0,0,1;0rad)
  sketch-geometry (8):
    g0: ArcOfCircle CenterX=23.7322 CenterY=-26.3322 CenterZ=0 NormalX=0 NormalY=0 NormalZ=1 AngleXU=0 Radius=1 StartAngle=0.58404 EndAngle=4.12835
    g1: ArcOfCircle CenterX=36.7322 CenterY=-26.3322 CenterZ=0 NormalX=0 NormalY=0 NormalZ=1 AngleXU=0 Radius=1 StartAngle=0.58404 EndAngle=4.12835
    g2: LineSegment [constr] StartX=25.5 StartY=-28.1 StartZ=0 EndX=23.7322 EndY=-26.3322 EndZ=0
    g3: LineSegment [constr] StartX=38.5 StartY=-28.1 StartZ=0 EndX=36.7322 EndY=-26.3322 EndZ=0
    g4: LineSegment [constr] StartX=25.5 StartY=-28.1 StartZ=0 EndX=28 EndY=-28.1 EndZ=0
    g5: LineSegment [constr] StartX=38.5 StartY=-28.1 StartZ=0 EndX=41 EndY=-28.1 EndZ=0
    g6: ArcOfCircle CenterX=25.5 CenterY=-28.1 CenterZ=0 NormalX=0 NormalY=0 NormalZ=1 AngleXU=0 Radius=2.5 StartAngle=1.95348 EndAngle=2.75891
    g7: ArcOfCircle CenterX=38.5 CenterY=-28.1 CenterZ=0 NormalX=0 NormalY=0 NormalZ=1 AngleXU=0 Radius=2.5 StartAngle=1.95348 EndAngle=2.75891
  constraints (24):
    c: PointOnObject(g0,g-4)
    c: PointOnObject(g1,g-3)
    c: Diameter(g0) = 2
    c: Diameter(g1) = 2
    c: Coincident(g2,g-4)
    c: Coincident(g2,g0)
    c: Coincident(g3,g-3)
    c: Coincident(g3,g1)
    c: Coincident(g4,g2)
    c: PointOnObject(g4,g-4)
    c: Horizontal(g4)
    c: Coincident(g5,g3)
    c: PointOnObject(g5,g-3)
    c: Horizontal(g5)
    c: Coincident(g6,g0)
    c: Coincident(g6,g0)
    c: Coincident(g7,g1)
    c: Coincident(g7,g1)
    c: Coincident(g6,g2)
    c: Coincident(g7,g3)
    c: Angle(g4,g2) = 2.35619
    c: Angle(g5,g3) = 2.35619
    c: PointOnObject(g1,g7)
    c: PointOnObject(g0,g6)
FEATURE [PartDesign::Pad] Pad012
  BaseFeature = -> Pad011
  Direction = (0,0,1)
  Length = 0.3
  Length2 = 10
  Profile = -> Sketch013
  ReferenceAxis = -> Sketch013 [N_Axis]
  Refine = true
  Suppressed = false
  Type = 0
FEATURE [Sketcher::SketchObject] Sketch014
  ArcFitTolerance = 1e-06
  AttachmentSupport = -> [Pad012]
  ExternalGeometry = -> [Pad012]
  FullyConstrained = true
  MakeInternals = false
  MapMode = 5
  Placement = pos=(0,0,2.3) rot=(0,0,1;0rad)
  sketch-geometry (2):
    g0: Circle CenterX=25.5 CenterY=-28.1 CenterZ=0 NormalX=0 NormalY=0 NormalZ=1 AngleXU=0 Radius=1.45
    g1: Circle CenterX=38.5 CenterY=-28.1 CenterZ=0 NormalX=0 NormalY=0 NormalZ=1 AngleXU=0 Radius=1.45
  constraints (4):
    c: Coincident(g0,g-3)
    c: Coincident(g1,g-4)
    c: Diameter(g0) = 2.9
    c: Diameter(g1) = 2.9
FEATURE [PartDesign::Pad] Pad013
  BaseFeature = -> Pad012
  Direction = (0,0,1)
  Length = 2
  Length2 = 10
  Profile = -> Sketch014
  ReferenceAxis = -> Sketch014 [N_Axis]
  Refine = true
  Suppressed = false
  Type = 0
FEATURE [Sketcher::SketchObject] Sketch015
  ArcFitTolerance = 1e-06
  AttachmentSupport = -> [Pad013]
  ExternalGeometry = -> [Pad013]
  FullyConstrained = true
  MakeInternals = false
  MapMode = 5
  Placement = pos=(0,-1e-16,0) rot=(0,0.707107,0.707107;3.14159rad)
  sketch-geometry (9):
    g0: LineSegment StartX=-30.8 StartY=11.2 StartZ=0 EndX=-30.8 EndY=6.2 EndZ=0
    g1: LineSegment StartX=-30.8 StartY=6.2 StartZ=0 EndX=-24.8 EndY=6.2 EndZ=0
    g2: LineSegment StartX=-24.8 StartY=6.2 StartZ=0 EndX=-24.8 EndY=11.2 EndZ=0
    g3: LineSegment StartX=-24.8 StartY=11.2 StartZ=0 EndX=-30.8 EndY=11.2 EndZ=0
    g4: LineSegment StartX=-36.0765 StartY=11.2 StartZ=0 EndX=-39.3191 EndY=2 EndZ=0
    g5: LineSegment StartX=-39.3191 StartY=2 StartZ=0 EndX=-34.3191 EndY=2 EndZ=0
    g6: LineSegment StartX=-34.3191 StartY=2 StartZ=0 EndX=-34.3191 EndY=11.2 EndZ=0
    g7: LineSegment StartX=-34.3191 StartY=11.2 StartZ=0 EndX=-36.0765 EndY=11.2 EndZ=0
    g8: LineSegment [constr] StartX=-37.0327 StartY=8.48709 StartZ=0 EndX=-39.8621 EndY=9.48434 EndZ=0
  constraints (28):
    c: Coincident(g0,g1)
    c: Coincident(g1,g2)
    c: Coincident(g2,g3)
    c: Coincident(g3,g0)
    c: Vertical(g0)
    c: Vertical(g2)
    c: Horizontal(g1)
    c: Horizontal(g3)
    c: Coincident(g5,g4)
    c: Horizontal(g5)
    c: Coincident(g6,g5)
    c: Vertical(g6)
    c: Coincident(g7,g6)
    c: Coincident(g7,g4)
    c: Horizontal(g7)
    c: DistanceY(g-6,g4) = 2
    c: DistanceY(g0,g0) = 5
    c: DistanceX(g3,g3) = 6
    c: DistanceX(g2,g-5) = 2.5
    c: DistanceY(g2,g-5) = 3
    c: DistanceY(g4,g-4) = 3
    c: Parallel(g4,g-4)
    c: DistanceX(g5,g5) = 5
    c: PointOnObject(g8,g4)
    c: PointOnObject(g8,g-4)
    c: Angle(g8,g4) = 1.5708
    c: Distance(g8,g-4) = 5
    c: Distance(g8) = 3
FEATURE [PartDesign::Pocket] Pocket001
  BaseFeature = -> Pad013
  Direction = (0,-1,2e-16)
  Length = 5
  Length2 = 5
  Profile = -> Sketch015
  ReferenceAxis = -> Sketch015 [N_Axis]
  Refine = true
  Suppressed = false
  Type = 0
FEATURE [Sketcher::SketchObject] Sketch016
  ArcFitTolerance = 1e-06
  AttachmentSupport = -> [Pocket001]
  ExternalGeometry = -> [Pocket001]
  FullyConstrained = true
  MakeInternals = false
  MapMode = 5
  Placement = pos=(0,-1e-16,0) rot=(0,0.707107,0.707107;3.14159rad)
  sketch-geometry (16):
    g0: LineSegment StartX=-37.2 StartY=12.5 StartZ=0 EndX=-23.3 EndY=12.5 EndZ=0
    g1: LineSegment StartX=-23.3 StartY=12.5 StartZ=0 EndX=-23.3 EndY=12 EndZ=0
    g2: LineSegment StartX=-23.3 StartY=12 StartZ=0 EndX=-24.3 EndY=12 EndZ=0
    g3: LineSegment StartX=-24.3 StartY=12 StartZ=0 EndX=-24.3 EndY=2 EndZ=0
    g4: LineSegment StartX=-24.3 StartY=2 StartZ=0 EndX=-24.8 EndY=2 EndZ=0
    g5: LineSegment StartX=-24.8 StartY=2 StartZ=0 EndX=-24.8 EndY=12 EndZ=0
    g6: LineSegment StartX=-24.8 StartY=12 StartZ=0 EndX=-32.6 EndY=12 EndZ=0
    g7: LineSegment StartX=-32.6 StartY=12 StartZ=0 EndX=-32.6 EndY=2 EndZ=0
    g8: LineSegment StartX=-32.6 StartY=2 StartZ=0 EndX=-33.1 EndY=2 EndZ=0
    g9: LineSegment StartX=-33.1 StartY=2 StartZ=0 EndX=-33.1 EndY=12 EndZ=0
    g10: LineSegment StartX=-33.1 StartY=12 StartZ=0 EndX=-37.2 EndY=12 EndZ=0
    g11: LineSegment StartX=-37.2 StartY=12.5 StartZ=0 EndX=-37.2 EndY=12 EndZ=0
    g12: LineSegment StartX=-30.35 StartY=3.95 StartZ=0 EndX=-30.35 EndY=3.2 EndZ=0
    g13: LineSegment StartX=-30.35 StartY=3.2 StartZ=0 EndX=-28.15 EndY=3.2 EndZ=0
    g14: LineSegment StartX=-28.15 StartY=3.2 StartZ=0 EndX=-28.15 EndY=3.95 EndZ=0
    g15: LineSegment StartX=-28.15 StartY=3.95 StartZ=0 EndX=-30.35 EndY=3.95 EndZ=0
  constraints (48):
    c: Horizontal(g0)
    c: Coincident(g1,g0)
    c: Vertical(g1)
    c: Coincident(g2,g1)
    c: Horizontal(g2)
    c: Coincident(g3,g2)
    c: Vertical(g3)
    c: Coincident(g4,g3)
    c: Coincident(g5,g4)
    c: Vertical(g5)
    c: Coincident(g6,g5)
    c: Horizontal(g6)
    c: Coincident(g7,g6)
    c: Vertical(g7)
    c: Coincident(g8,g7)
    c: Coincident(g9,g8)
    c: Vertical(g9)
    c: Coincident(g10,g9)
    c: Horizontal(g10)
    c: Coincident(g11,g0)
    c: Coincident(g11,g10)
    c: Vertical(g11)
    c: Coincident(g12,g13)
    c: Coincident(g13,g14)
    c: Coincident(g14,g15)
    c: Coincident(g15,g12)
    c: Vertical(g12)
    c: Vertical(g14)
    c: Horizontal(g13)
    c: Horizontal(g15)
    c: Horizontal(g8)
    c: Horizontal(g4)
    c: DistanceY(g8,g-3) = 0
    c: DistanceX(g8,g8) = 0.5
    c: DistanceX(g4,g4) = 0.5
    c: DistanceY(g11,g11) = 0.5
    c: DistanceY(g1,g1) = 0.5
    c: DistanceY(g5,g0) = 0.5
    c: DistanceX(g0,g-4) = 1
    c: DistanceY(g7,g4) = 0
    c: DistanceX(g-5,g0) = 1
    c: DistanceY(g0,g-5) = 1.7
    c: PointOnObject(g-6,g5)
    c: DistanceX(g7,g4) = 7.8
    c: DistanceX(g15,g15) = 2.2
    c: DistanceY(g14,g14) = 0.75
    c: DistanceX(g7,g12) = 2.25
    c: DistanceY(g12,g-7) = 2.25
FEATURE [PartDesign::Pad] Pad014
  BaseFeature = -> Pocket001
  Direction = (0,1,-2e-16)
  Length = 0.3
  Length2 = 10
  Profile = -> Sketch016
  ReferenceAxis = -> Sketch016 [N_Axis]
  Refine = true
  Suppressed = false
  Type = 0
FEATURE [Sketcher::SketchObject] Sketch017
  ArcFitTolerance = 1e-06
  AttachmentSupport = -> [Pad014]
  ExternalGeometry = -> [Pad014]
  FullyConstrained = true
  MakeInternals = false
  MapMode = 5
  Placement = pos=(0,0,0) rot=(1,0,0;3.14159rad)
  sketch-geometry (14):
    g0: LineSegment StartX=40.75 StartY=0 StartZ=0 EndX=44.5 EndY=0 EndZ=0
    g1: LineSegment StartX=44.5 StartY=0 StartZ=0 EndX=44.5 EndY=11 EndZ=0
    g2: LineSegment StartX=44.5 StartY=11 StartZ=0 EndX=30.5 EndY=11 EndZ=0
    g3: LineSegment StartX=30.5 StartY=11 StartZ=0 EndX=30.5 EndY=9 EndZ=0
    g4: LineSegment StartX=30.5 StartY=9 StartZ=0 EndX=42.5 EndY=9 EndZ=0
    g5: LineSegment StartX=42.5 StartY=9 StartZ=0 EndX=42.5 EndY=2 EndZ=0
    g6: LineSegment StartX=42.5 StartY=2 StartZ=0 EndX=40.75 EndY=2 EndZ=0
    g7: LineSegment StartX=40.75 StartY=2 StartZ=0 EndX=40.75 EndY=0 EndZ=0
    g8: LineSegment StartX=42.5 StartY=32 StartZ=0 EndX=42.5 EndY=21.5 EndZ=0
    g9: LineSegment StartX=42.5 StartY=21.5 StartZ=0 EndX=30.5 EndY=21.5 EndZ=0
    g10: LineSegment StartX=30.5 StartY=21.5 StartZ=0 EndX=30.5 EndY=23.5 EndZ=0
    g11: LineSegment StartX=30.5 StartY=23.5 StartZ=0 EndX=40.5 EndY=23.5 EndZ=0
    g12: LineSegment StartX=40.5 StartY=23.5 StartZ=0 EndX=40.5 EndY=32 EndZ=0
    g13: LineSegment StartX=40.5 StartY=32 StartZ=0 EndX=42.5 EndY=32 EndZ=0
  constraints (36):
    c: PointOnObject(g0,g-9)
    c: Coincident(g0,g-9)
    c: Coincident(g1,g0)
    c: Coincident(g1,g-7)
    c: Coincident(g2,g1)
    c: PointOnObject(g2,g-6)
    c: Coincident(g3,g2)
    c: PointOnObject(g3,g-10)
    c: Vertical(g3)
    c: Coincident(g4,g3)
    c: Coincident(g4,g-10)
    c: Coincident(g5,g4)
    c: Coincident(g5,g-11)
    c: Coincident(g6,g5)
    c: PointOnObject(g6,g-11)
    c: Coincident(g7,g6)
    c: Coincident(g7,g0)
    c: Vertical(g7)
    c: Coincident(g8,g-4)
    c: Coincident(g8,g-5)
    c: Coincident(g9,g8)
    c: PointOnObject(g9,g-5)
    c: Coincident(g10,g9)
    c: Vertical(g10)
    c: Coincident(g11,g10)
    c: Horizontal(g11)
    c: Coincident(g12,g11)
    c: PointOnObject(g12,g-4)
    c: Vertical(g12)
    c: Coincident(g13,g12)
    c: Coincident(g13,g8)
    c: DistanceX(g13,g13) = 2
    c: DistanceY(g10,g10) = 2
    c: DistanceX(g10,g11) = 10
    c: DistanceX(g9,g2) = 0
    c: DistanceX(g6,g6) = 1.75
FEATURE [PartDesign::Pad] Pad015
  BaseFeature = -> Pad014
  Direction = (0,0,-1)
  Length = 8.2
  Length2 = 10
  Profile = -> Sketch017
  ReferenceAxis = -> Sketch017 [N_Axis]
  Refine = true
  Suppressed = false
  Type = 0
FEATURE [Sketcher::SketchObject] Sketch018
  ArcFitTolerance = 1e-06
  AttachmentSupport = -> [Pad015]
  ExternalGeometry = -> [Pad015]
  FullyConstrained = true
  MakeInternals = false
  MapMode = 5
  Placement = pos=(0,0,0) rot=(1,0,0;3.14159rad)
  sketch-geometry (1):
    g0: Circle CenterX=20.6 CenterY=16.25 CenterZ=0 NormalX=0 NormalY=0 NormalZ=1 AngleXU=0 Radius=4.95
  constraints (2):
    c: Coincident(g0,g-3)
    c: Diameter(g0) = 9.9
FEATURE [PartDesign::Pad] Pad016
  BaseFeature = -> Pad015
  Direction = (0,0,-1)
  Length = 2.5
  Length2 = 10
  Profile = -> Sketch018
  ReferenceAxis = -> Sketch018 [N_Axis]
  Refine = true
  Suppressed = false
  Type = 0
FEATURE [Sketcher::SketchObject] Sketch019
  ArcFitTolerance = 1e-06
  AttachmentSupport = -> [Pad016]
  ExternalGeometry = -> [Pad016]
  FullyConstrained = true
  MakeInternals = false
  MapMode = 5
  Placement = pos=(0,-23.5,0) rot=(1,0,0;1.5708rad)
  sketch-geometry (4):
    g0: LineSegment StartX=30.5 StartY=-8.2 StartZ=0 EndX=23.6194 EndY=1.8e-15 EndZ=0
    g1: LineSegment StartX=30.5 StartY=-8.2 StartZ=0 EndX=33.8806 EndY=-8.2 EndZ=0
    g2: LineSegment StartX=33.8806 StartY=-8.2 StartZ=0 EndX=27 EndY=0 EndZ=0
    g3: LineSegment StartX=27 StartY=7e-16 StartZ=0 EndX=23.6194 EndY=2.1e-15 EndZ=0
  constraints (10):
    c: Coincident(g0,g-3)
    c: Angle(g-3,g0) = 0.698132
    c: PointOnObject(g0,g-4)
    c: Coincident(g1,g0)
    c: Horizontal(g1)
    c: Coincident(g2,g1)
    c: Parallel(g0,g2)
    c: Coincident(g3,g2)
    c: Coincident(g3,g0)
    c: Coincident(g2,g-5)
FEATURE [PartDesign::Pad] Pad017
  BaseFeature = -> Pad016
  Direction = (0,-1,2e-16)
  Length = 14.5
  Length2 = 10
  Profile = -> Sketch019
  ReferenceAxis = -> Sketch019 [N_Axis]
  Refine = true
  Reversed = true
  Suppressed = false
  Type = 0
FEATURE [Sketcher::SketchObject] Sketch020
  ArcFitTolerance = 1e-06
  AttachmentSupport = -> [Pad017]
  ExternalGeometry = -> [Pad017]
  FullyConstrained = true
  MakeInternals = false
  MapMode = 5
  Placement = pos=(0,-9,0) rot=(0,0.707107,0.707107;3.14159rad)
  sketch-geometry (3):
    g0: LineSegment StartX=-30.5 StartY=0 StartZ=0 EndX=-30.5 EndY=-4.17114 EndZ=0
    g1: LineSegment StartX=-30.5 StartY=-4.17114 StartZ=0 EndX=-27 EndY=0 EndZ=0
    g2: LineSegment StartX=-27 StartY=0 StartZ=0 EndX=-30.5 EndY=0 EndZ=0
  constraints (6):
    c: Coincident(g0,g-4)
    c: Coincident(g0,g-3)
    c: Coincident(g1,g0)
    c: Coincident(g1,g-4)
    c: Coincident(g2,g1)
    c: Coincident(g2,g0)
FEATURE [PartDesign::Pad] Pad018
  BaseFeature = -> Pad017
  Direction = (0,1,-2e-16)
  Length = 2
  Length2 = 10
  Profile = -> Sketch020
  ReferenceAxis = -> Sketch020 [N_Axis]
  Refine = true
  Reversed = true
  Suppressed = false
  Type = 0
FEATURE [Sketcher::SketchObject] Sketch021
  ArcFitTolerance = 1e-06
  AttachmentSupport = -> [Pad018]
  ExternalGeometry = -> [Pad018]
  FullyConstrained = true
  MakeInternals = false
  MapMode = 5
  Placement = pos=(0,-23.5,0) rot=(1,0,0;1.5708rad)
  sketch-geometry (3):
    g0: LineSegment StartX=30.5 StartY=0 StartZ=0 EndX=27 EndY=0 EndZ=0
    g1: LineSegment StartX=27 StartY=0 StartZ=0 EndX=30.5 EndY=-4.17114 EndZ=0
    g2: LineSegment StartX=30.5 StartY=-4.17114 StartZ=0 EndX=30.5 EndY=0 EndZ=0
  constraints (6):
    c: Coincident(g0,g-3)
    c: Coincident(g0,g-4)
    c: Coincident(g1,g0)
    c: Coincident(g1,g-4)
    c: Coincident(g2,g1)
    c: Coincident(g2,g0)
FEATURE [PartDesign::Pad] Pad019
  BaseFeature = -> Pad018
  Direction = (0,-1,2e-16)
  Length = 2
  Length2 = 10
  Profile = -> Sketch021
  ReferenceAxis = -> Sketch021 [N_Axis]
  Refine = true
  Reversed = true
  Suppressed = false
  Type = 0
FEATURE [Sketcher::SketchObject] Sketch022
  ArcFitTolerance = 1e-06
  AttachmentSupport = -> [Pad019]
  ExternalGeometry = -> [Pad019]
  FullyConstrained = true
  MakeInternals = false
  MapMode = 5
  Placement = pos=(0,0,0) rot=(1,0,0;3.14159rad)
  sketch-geometry (4):
    g0: LineSegment StartX=6.7 StartY=19.45 StartZ=0 EndX=6.7 EndY=7.55 EndZ=0
    g1: LineSegment StartX=6.7 StartY=7.55 StartZ=0 EndX=10.9 EndY=7.55 EndZ=0
    g2: LineSegment StartX=10.9 StartY=7.55 StartZ=0 EndX=10.9 EndY=19.45 EndZ=0
    g3: LineSegment StartX=10.9 StartY=19.45 StartZ=0 EndX=6.7 EndY=19.45 EndZ=0
  constraints (14):
    c: Coincident(g0,g1)
    c: Coincident(g1,g2)
    c: Coincident(g2,g3)
    c: Coincident(g3,g0)
    c: Vertical(g0)
    c: Vertical(g2)
    c: Horizontal(g1)
    c: Horizontal(g3)
    c: DistanceY(g0,g0) = 11.9
    c: DistanceX(g3,g3) = 4.2
    c: DistanceY(g-5,g-3) = 15
    c: DistanceX(g-6,g-4) = 7
    c: DistanceX(g-6,g0) = 1.4
    c: DistanceY(g2,g-3) = 1.55
FEATURE [PartDesign::Pocket] Pocket002
  BaseFeature = -> Pad019
  Direction = (0,0,1)
  Length = 2
  Length2 = 5
  Profile = -> Sketch022
  ReferenceAxis = -> Sketch022 [N_Axis]
  Refine = true
  Suppressed = false
  Type = 0
FEATURE [PartDesign::Body] Body  label="Rear_Torso"
  AllowCompound = false
  Group = -> [Sketch,Pad,Sketch001,Pad001,Sketch002,Pad002,Sketch003,Pad003,Sketch004,Pad004,Sketch005,Pad005,Sketch006,Pad006,Sketch007,Pad007,Fillet,Sketch008,Pad008,Sketch009,Pad009,Sketch010,Pocket,Sketch011,Pad010,Sketch012,Pad011,Sketch013,Pad012,Sketch014,Pad013,Sketch015,Pocket001,Sketch016,Pad014,Sketch017,Pad015,Sketch018,Pad016,Sketch019,Pad017,Sketch020,Pad018,Sketch021,Pad019,Sketch022,Pocket002,+48 more]
  Origin = -> Origin
  Tip = -> Pad101
COMPONENT P1 — recipe-attached ("Front_Torso", modeled in this document).
Construction recipe (the document's own serialized feature program — sketch geometry with constraints, then the solid features built on it; lengths are millimeters unless a unit is written):

FEATURE [PartDesign::SubShapeBinder] Binder
  BindCopyOnChange = 0
  BindMode = 2
  ClaimChildren = false
  Context = -> Body001 [Binder.]
  Fuse = false
  MakeFace = true
  OffsetFill = false
  OffsetIntersection = false
  OffsetJoinType = 0
  OffsetOpenResult = false
  PartialLoad = false
  Refine = true
  Relative = true
  _Version = 2
FEATURE [Sketcher::SketchObject] Sketch045
  ArcFitTolerance = 1e-06
  AttachmentSupport = -> [Binder]
  ExternalGeometry = -> [Binder]
  FullyConstrained = true
  MakeInternals = false
  MapMode = 5
  Placement = pos=(0,0,0) rot=(1,0,0;3.14159rad)
  sketch-geometry (8):
    g0: LineSegment StartX=3.5 StartY=24.5 StartZ=0 EndX=40 EndY=24.5 EndZ=0
    g1: LineSegment StartX=40 StartY=24.5 StartZ=0 EndX=40 EndY=32 EndZ=0
    g2: LineSegment StartX=40 StartY=32 StartZ=0 EndX=38.5 EndY=32 EndZ=0
    g3: LineSegment StartX=38.5 StartY=32 StartZ=0 EndX=38.5 EndY=26 EndZ=0
    g4: LineSegment StartX=2 StartY=26 StartZ=0 EndX=38.5 EndY=26 EndZ=0
    g5: LineSegment StartX=2 StartY=26 StartZ=0 EndX=2 EndY=20.5 EndZ=0
    g6: LineSegment StartX=2 StartY=20.5 StartZ=0 EndX=3.5 EndY=20.5 EndZ=0
    g7: LineSegment StartX=3.5 StartY=20.5 StartZ=0 EndX=3.5 EndY=24.5 EndZ=0
  constraints (23):
    c: Horizontal(g0)
    c: Coincident(g1,g0)
    c: Vertical(g1)
    c: Coincident(g2,g1)
    c: Horizontal(g2)
    c: Coincident(g3,g2)
    c: Vertical(g3)
    c: Horizontal(g4)
    c: Coincident(g4,g3)
    c: Coincident(g5,g4)
    c: Vertical(g5)
    c: Coincident(g6,g5)
    c: Horizontal(g6)
    c: Coincident(g7,g6)
    c: Coincident(g0,g7)
    c: Vertical(g7)
    c: DistanceY(g4,g-20) = 6
    c: DistanceY(g0,g3) = 1.5
    c: DistanceX(g2,g1) = 1.5
    c: PointOnObject(g2,g-3)
    c: DistanceX(g6,g6) = 1.5
    c: Coincident(g5,g-22)
    c: DistanceX(g4,g4) = 36.5
FEATURE [PartDesign::Pad] Pad029
  Direction = (0,0,-1)
  Length = 8.2
  Length2 = 10
  Profile = -> Sketch045
  ReferenceAxis = -> Sketch045 [N_Axis]
  Refine = true
  Suppressed = false
  Type = 0
FEATURE [Sketcher::SketchObject] Sketch046
  ArcFitTolerance = 1e-06
  AttachmentSupport = -> [Pad029]
  ExternalGeometry = -> [Pad029]
  FullyConstrained = true
  MakeInternals = false
  MapMode = 5
  Placement = pos=(0,-26,0) rot=(1,0,0;1.5708rad)
  sketch-geometry (6):
    g0: LineSegment StartX=9 StartY=0 StartZ=0 EndX=9 EndY=-4 EndZ=0
    g1: LineSegment StartX=13 StartY=0 StartZ=0 EndX=13 EndY=-4 EndZ=0
    g2: ArcOfCircle CenterX=11 CenterY=-4 CenterZ=0 NormalX=0 NormalY=0 NormalZ=1 AngleXU=0 Radius=2 StartAngle=3.14159 EndAngle=6.28319
    g3: LineSegment StartX=9 StartY=0 StartZ=0 EndX=13 EndY=0 EndZ=0
    g4: LineSegment [constr] StartX=9 StartY=-4 StartZ=0 EndX=13 EndY=-4 EndZ=0
    g5: LineSegment [constr] StartX=11 StartY=-4 StartZ=0 EndX=11 EndY=-6 EndZ=0
  constraints (18):
    c: PointOnObject(g0,g-3)
    c: Vertical(g0)
    c: PointOnObject(g1,g-3)
    c: Vertical(g1)
    c: Coincident(g2,g0)
    c: Coincident(g2,g1)
    c: Coincident(g3,g0)
    c: Coincident(g3,g1)
    c: Coincident(g4,g0)
    c: Coincident(g4,g1)
    c: Horizontal(g4)
    c: PointOnObject(g2,g4)
    c: Diameter(g2) = 4
    c: DistanceX(g-5,g0) = 7
    c: Coincident(g5,g2)
    c: PointOnObject(g5,g2)
    c: Vertical(g5)
    c: DistanceY(g5,g0) = 6
FEATURE [PartDesign::Pocket] Pocket017
  BaseFeature = -> Pad029
  Direction = (0,1,-2e-16)
  Length = 5
  Length2 = 5
  Profile = -> Sketch046
  ReferenceAxis = -> Sketch046 [N_Axis]
  Refine = true
  Suppressed = false
  Type = 0
FEATURE [Sketcher::SketchObject] Sketch047
  ArcFitTolerance = 1e-06
  AttachmentSupport = -> [Pocket017]
  ExternalGeometry = -> [Pocket017]
  FullyConstrained = true
  MakeInternals = false
  MapMode = 5
  Placement = pos=(0,0,-8.2) rot=(1,0,0;3.14159rad)
  sketch-geometry (24):
    g0: LineSegment StartX=38.5 StartY=32 StartZ=0 EndX=38.5 EndY=26 EndZ=0
    g1: LineSegment StartX=38.5 StartY=26 StartZ=0 EndX=26.5 EndY=26 EndZ=0
    g2: LineSegment StartX=26.5 StartY=26 StartZ=0 EndX=20.5 EndY=32 EndZ=0
    g3: LineSegment StartX=20.5 StartY=32 StartZ=0 EndX=2 EndY=32 EndZ=0
    g4: LineSegment StartX=2 StartY=32 StartZ=0 EndX=2 EndY=20.5 EndZ=0
    g5: LineSegment StartX=2 StartY=20.5 StartZ=0 EndX=6.8 EndY=20.5 EndZ=0
    g6: LineSegment StartX=6.8 StartY=20.5 StartZ=0 EndX=6.8 EndY=11.75 EndZ=0
    g7: LineSegment StartX=6.8 StartY=11.75 StartZ=0 EndX=2 EndY=11.75 EndZ=0
    g8: LineSegment StartX=2 StartY=11.75 StartZ=0 EndX=2 EndY=0 EndZ=0
    g9: LineSegment StartX=2 StartY=0 StartZ=0 EndX=20.5 EndY=0 EndZ=0
    g10: LineSegment StartX=20.5 StartY=0 StartZ=0 EndX=26.5 EndY=6 EndZ=0
    g11: LineSegment StartX=26.5 StartY=6 StartZ=0 EndX=38.5 EndY=6 EndZ=0
    g12: LineSegment StartX=38.5 StartY=6 StartZ=0 EndX=38.5 EndY=0 EndZ=0
    g13: LineSegment StartX=38.5 StartY=0 StartZ=0 EndX=42.5 EndY=0 EndZ=0
    g14: LineSegment StartX=42.5 StartY=0 StartZ=0 EndX=47.7 EndY=5.2 EndZ=0
    g15: LineSegment StartX=47.7 StartY=5.2 StartZ=0 EndX=47.7 EndY=9.2 EndZ=0
    g16: LineSegment StartX=47.7 StartY=9.2 StartZ=0 EndX=50.7 EndY=9.2 EndZ=0
    g17: LineSegment StartX=50.7 StartY=9.2 StartZ=0 EndX=55.8 EndY=14.3 EndZ=0
    g18: LineSegment StartX=55.8 StartY=14.3 StartZ=0 EndX=55.8 EndY=17.7 EndZ=0
    g19: LineSegment StartX=55.8 StartY=17.7 StartZ=0 EndX=50.7 EndY=22.8 EndZ=0
    g20: LineSegment StartX=50.7 StartY=22.8 StartZ=0 EndX=47.7 EndY=22.8 EndZ=0
    g21: LineSegment StartX=47.7 StartY=22.8 StartZ=0 EndX=47.7 EndY=26.8 EndZ=0
    g22: LineSegment StartX=42.5 StartY=32 StartZ=0 EndX=47.7 EndY=26.8 EndZ=0
    g23: LineSegment StartX=38.5 StartY=32 StartZ=0 EndX=42.5 EndY=32 EndZ=0
  constraints (71):
    c: Coincident(g0,g-3)
    c: Coincident(g0,g-4)
    c: Coincident(g1,g0)
    c: PointOnObject(g1,g-4)
    c: Coincident(g2,g1)
    c: Coincident(g3,g2)
    c: Horizontal(g3)
    c: Coincident(g4,g3)
    c: Coincident(g4,g-6)
    c: Vertical(g4)
    c: Coincident(g5,g4)
    c: Horizontal(g5)
    c: Coincident(g6,g5)
    c: Vertical(g6)
    c: Coincident(g7,g6)
    c: Horizontal(g7)
    c: Coincident(g8,g7)
    c: PointOnObject(g8,g-1)
    c: Vertical(g8)
    c: Coincident(g9,g8)
    c: PointOnObject(g9,g-1)
    c: Coincident(g10,g9)
    c: Coincident(g11,g10)
    c: Horizontal(g11)
    c: Coincident(g12,g11)
    c: PointOnObject(g12,g-1)
    c: Vertical(g12)
    c: Coincident(g13,g12)
    c: PointOnObject(g13,g-1)
    c: Coincident(g14,g13)
    c: Coincident(g15,g14)
    c: Vertical(g15)
    c: Coincident(g16,g15)
    c: Horizontal(g16)
    c: Coincident(g17,g16)
    c: Coincident(g18,g17)
    c: Vertical(g18)
    c: Coincident(g19,g18)
    c: Coincident(g20,g19)
    c: Horizontal(g20)
    c: Coincident(g21,g20)
    c: Vertical(g21)
    c: Coincident(g22,g21)
    c: DistanceY(g8,g8) = 11.75
    c: DistanceY(g4,g4) = 11.5
    c: DistanceX(g4,g5) = 4.8
    c: Angle(g10,g9) = 2.35619
    c: Angle(g3,g2) = 2.35619
    c: DistanceX(g1,g1) = 12
    c: DistanceX(g11,g11) = 12
    c: DistanceY(g0,g0) = 6
    c: DistanceY(g12,g12) = 6
    c: Coincident(g23,g0)
    c: Coincident(g23,g22)
    c: Horizontal(g23)
    c: DistanceX(g23,g23) = 4
    c: DistanceX(g13,g13) = 4
    c: DistanceX(g3,g3) = 18.5
    c: DistanceX(g9,g9) = 18.5
    c: DistanceX(g7,g7) = 4.8
    c: DistanceX(g3,g18) = 53.8
    c: DistanceY(g15,g15) = 4
    c: DistanceY(g21,g21) = 4
    c: DistanceX(g20,g20) = 3
    c: DistanceX(g16,g16) = 3
    c: DistanceX(g22,g21) = 5.2
    c: DistanceX(g13,g14) = 5.2
    c: Angle(g14,g13) = 2.35619
    c: Angle(g23,g22) = 2.35619
    c: Angle(g20,g19) = 2.35619
    c: Angle(g17,g16) = 2.35619
FEATURE [PartDesign::Pad] Pad030
  BaseFeature = -> Pocket017
  Direction = (0,0,-1)
  Length = 2
  Length2 = 10
  Profile = -> Sketch047
  ReferenceAxis = -> Sketch047 [N_Axis]
  Refine = true
  Suppressed = false
  Type = 0
FEATURE [PartDesign::Fillet] Fillet001
  Base = -> Pad030 [Edge77,Edge79]
  BaseFeature = -> Pad030
  Radius = 4
  Refine = true
  SupportTransform = false
  Suppressed = false
  UseAllEdges = false
FEATURE [Sketcher::SketchObject] Sketch048
  ArcFitTolerance = 1e-06
  AttachmentSupport = -> [Fillet001]
  ExternalGeometry = -> [Fillet001]
  FullyConstrained = true
  MakeInternals = false
  MapMode = 5
  Placement = pos=(0,0,-8.2) rot=(0,0,1;0rad)
  sketch-geometry (8):
    g0: LineSegment StartX=2 StartY=-11.75 StartZ=0 EndX=2 EndY=-6 EndZ=0
    g1: LineSegment StartX=2 StartY=-6 StartZ=0 EndX=38.5 EndY=-6 EndZ=0
    g2: LineSegment StartX=38.5 StartY=-6 StartZ=0 EndX=38.5 EndY=0 EndZ=0
    g3: LineSegment StartX=38.5 StartY=0 StartZ=0 EndX=40 EndY=0 EndZ=0
    g4: LineSegment StartX=40 StartY=0 StartZ=0 EndX=40 EndY=-7.5 EndZ=0
    g5: LineSegment StartX=40 StartY=-7.5 StartZ=0 EndX=3.5 EndY=-7.5 EndZ=0
    g6: LineSegment StartX=3.5 StartY=-7.5 StartZ=0 EndX=3.5 EndY=-11.75 EndZ=0
    g7: LineSegment StartX=3.5 StartY=-11.75 StartZ=0 EndX=2 EndY=-11.75 EndZ=0
  constraints (28):
    c: DistanceX(g-7,g-7) = 1.5
    c: DistanceX(g-3,g-3) = 1.5
    c: DistanceX(g-4,g-4) = 27
    c: DistanceX(g-9,g-9) = 4
    c: DistanceX(g-8,g-8) = 5.5
    c: DistanceY(g-10,g-10) = 6
    c: DistanceY(g-11,g-11) = 6
    c: Coincident(g0,g-13)
    c: PointOnObject(g0,g-12)
    c: Coincident(g1,g0)
    c: Coincident(g1,g-16)
    c: Horizontal(g1)
    c: Coincident(g2,g1)
    c: Coincident(g2,g-10)
    c: Coincident(g3,g2)
    c: PointOnObject(g3,g-1)
    c: Coincident(g4,g3)
    c: Vertical(g4)
    c: Coincident(g5,g4)
    c: Horizontal(g5)
    c: Coincident(g6,g5)
    c: PointOnObject(g6,g-13)
    c: Vertical(g6)
    c: Coincident(g7,g6)
    c: Coincident(g7,g0)
    c: DistanceX(g7,g7) = 1.5
    c: DistanceX(g3,g3) = 1.5
    c: DistanceY(g4,g1) = 1.5
FEATURE [PartDesign::Pad] Pad031
  BaseFeature = -> Fillet001
  Direction = (0,0,1)
  Length = 8.2
  Length2 = 10
  Profile = -> Sketch048
  ReferenceAxis = -> Sketch048 [N_Axis]
  Refine = true
  Suppressed = false
  Type = 0
FEATURE [Sketcher::SketchObject] Sketch049
  ArcFitTolerance = 1e-06
  AttachmentSupport = -> [Pad031]
  ExternalGeometry = -> [Pad031]
  FullyConstrained = true
  MakeInternals = false
  MapMode = 5
  Placement = pos=(0,-6,0) rot=(0,0.707107,0.707107;3.14159rad)
  sketch-geometry (4):
    g0: LineSegment StartX=-13 StartY=0 StartZ=0 EndX=-9 EndY=0 EndZ=0
    g1: LineSegment StartX=-9 StartY=0 StartZ=0 EndX=-9 EndY=-4 EndZ=0
    g2: LineSegment StartX=-13 StartY=0 StartZ=0 EndX=-13 EndY=-4 EndZ=0
    g3: ArcOfCircle CenterX=-11 CenterY=-4.00001 CenterZ=0 NormalX=0 NormalY=0 NormalZ=1 AngleXU=0 Radius=2 StartAngle=3.14159 EndAngle=6.28319
  constraints (9):
    c: Coincident(g0,g-3)
    c: Coincident(g0,g-4)
    c: Coincident(g1,g0)
    c: Coincident(g1,g-5)
    c: Coincident(g2,g0)
    c: Coincident(g2,g-5)
    c: Coincident(g3,g2)
    c: Coincident(g3,g1)
    c: Tangent(g3,g-5)
FEATURE [PartDesign::Pocket] Pocket018
  BaseFeature = -> Pad031
  Direction = (0,-1,2e-16)
  Length = 5
  Length2 = 5
  Profile = -> Sketch049
  ReferenceAxis = -> Sketch049 [N_Axis]
  Refine = true
  Suppressed = false
  Type = 0
FEATURE [Sketcher::SketchObject] Sketch050
  ArcFitTolerance = 1e-06
  AttachmentSupport = -> [Pocket018]
  ExternalGeometry = -> [Pocket018]
  FullyConstrained = true
  MakeInternals = false
  MapMode = 5
  sketch-geometry (8):
    g0: LineSegment StartX=2 StartY=-6.05 StartZ=0 EndX=2 EndY=-9.05 EndZ=0
    g1: LineSegment StartX=2 StartY=-9.05 StartZ=0 EndX=3.5 EndY=-9.05 EndZ=0
    g2: LineSegment StartX=3.5 StartY=-9.05 StartZ=0 EndX=3.5 EndY=-6.05 EndZ=0
    g3: LineSegment StartX=3.5 StartY=-6.05 StartZ=0 EndX=2 EndY=-6.05 EndZ=0
    g4: LineSegment StartX=3.5 StartY=-26 StartZ=0 EndX=3.5 EndY=-23 EndZ=0
    g5: LineSegment StartX=3.5 StartY=-23 StartZ=0 EndX=2 EndY=-23 EndZ=0
    g6: LineSegment StartX=2 StartY=-23 StartZ=0 EndX=2 EndY=-26 EndZ=0
    g7: LineSegment StartX=2 StartY=-26 StartZ=0 EndX=3.5 EndY=-26 EndZ=0
  constraints (23):
    c: Coincident(g0,g1)
    c: Coincident(g1,g2)
    c: Coincident(g2,g3)
    c: Coincident(g3,g0)
    c: Vertical(g0)
    c: Vertical(g2)
    c: Horizontal(g1)
    c: Horizontal(g3)
    c: PointOnObject(g0,g-6)
    c: PointOnObject(g1,g-7)
    c: Coincident(g4,g5)
    c: Coincident(g5,g6)
    c: Coincident(g6,g7)
    c: Vertical(g4)
    c: Vertical(g6)
    c: Horizontal(g5)
    c: Horizontal(g7)
    c: Distance(g4) = 3
    c: Distance(g0) = 3
    c: DistanceY(g0,g-6) = 0.05
    c: Coincident(g4,g7)
    c: DistanceX(g6,g4) = 1.5
    c: Coincident(g6,g-4)
FEATURE [PartDesign::Pad] Pad032
  BaseFeature = -> Pocket018
  Direction = (0,0,1)
  Length = 0.1
  Length2 = 10
  Profile = -> Sketch050
  ReferenceAxis = -> Sketch050 [N_Axis]
  Refine = true
  Suppressed = false
  Type = 0
FEATURE [Sketcher::SketchObject] Sketch051
  ArcFitTolerance = 1e-06
  AttachmentSupport = -> [Pad032]
  ExternalGeometry = -> [Pad032]
  FullyConstrained = true
  MakeInternals = false
  MapMode = 5
  Placement = pos=(0,0,0.1) rot=(0,0,1;0rad)
  sketch-geometry (8):
    g0: LineSegment StartX=3.5 StartY=-23 StartZ=0 EndX=0.5 EndY=-23 EndZ=0
    g1: LineSegment StartX=0.5 StartY=-23 StartZ=0 EndX=0.5 EndY=-26 EndZ=0
    g2: LineSegment StartX=0.5 StartY=-26 StartZ=0 EndX=3.5 EndY=-26 EndZ=0
    g3: LineSegment StartX=3.5 StartY=-26 StartZ=0 EndX=3.5 EndY=-23 EndZ=0
    g4: LineSegment StartX=3.5 StartY=-6.05 StartZ=0 EndX=0.5 EndY=-6.05 EndZ=0
    g5: LineSegment StartX=0.5 StartY=-6.05 StartZ=0 EndX=0.5 EndY=-9.05 EndZ=0
    g6: LineSegment StartX=0.5 StartY=-9.05 StartZ=0 EndX=3.5 EndY=-9.05 EndZ=0
    g7: LineSegment StartX=3.5 StartY=-9.05 StartZ=0 EndX=3.5 EndY=-6.05 EndZ=0
  constraints (20):
    c: Coincident(g0,g1)
    c: Coincident(g1,g2)
    c: Coincident(g2,g3)
    c: Coincident(g3,g0)
    c: Horizontal(g0)
    c: Horizontal(g2)
    c: Vertical(g1)
    c: Coincident(g0,g-10)
    c: Coincident(g4,g5)
    c: Coincident(g5,g6)
    c: Coincident(g6,g7)
    c: Coincident(g7,g4)
    c: Horizontal(g4)
    c: Horizontal(g6)
    c: Vertical(g5)
    c: Coincident(g4,g-4)
    c: Coincident(g6,g-6)
    c: Coincident(g2,g-8)
    c: DistanceX(g2,g2) = 3
    c: DistanceX(g6,g6) = 3
FEATURE [PartDesign::Pad] Pad033
  BaseFeature = -> Pad032
  Direction = (0,0,1)
  Length = 1.5
  Length2 = 10
  Profile = -> Sketch051
  ReferenceAxis = -> Sketch051 [N_Axis]
  Refine = true
  Suppressed = false
  Type = 0
FEATURE [Sketcher::SketchObject] Sketch052
  ArcFitTolerance = 1e-06
  AttachmentSupport = -> [Pad033]
  ExternalGeometry = -> [Pad033]
  FullyConstrained = true
  MakeInternals = false
  MapMode = 5
  Placement = pos=(0,0,-8.2) rot=(0,0,1;0rad)
  sketch-geometry (8):
    g0: LineSegment StartX=3.5 StartY=-20.5 StartZ=0 EndX=3.5 EndY=-22.5 EndZ=0
    g1: LineSegment StartX=3.5 StartY=-22.5 StartZ=0 EndX=8 EndY=-22.5 EndZ=0
    g2: LineSegment StartX=8 StartY=-22.5 StartZ=0 EndX=8 EndY=-20.5 EndZ=0
    g3: LineSegment StartX=8 StartY=-20.5 StartZ=0 EndX=3.5 EndY=-20.5 EndZ=0
    g4: LineSegment StartX=3.5 StartY=-11.75 StartZ=0 EndX=8 EndY=-11.75 EndZ=0
    g5: LineSegment StartX=8 StartY=-11.75 StartZ=0 EndX=8 EndY=-9.75 EndZ=0
    g6: LineSegment StartX=8 StartY=-9.75 StartZ=0 EndX=3.5 EndY=-9.75 EndZ=0
    g7: LineSegment StartX=3.5 StartY=-9.75 StartZ=0 EndX=3.5 EndY=-11.75 EndZ=0
  constraints (22):
    c: Coincident(g0,g1)
    c: Coincident(g1,g2)
    c: Coincident(g2,g3)
    c: Coincident(g3,g0)
    c: Vertical(g0)
    c: Vertical(g2)
    c: Horizontal(g1)
    c: Horizontal(g3)
    c: Coincident(g0,g-8)
    c: Coincident(g4,g5)
    c: Coincident(g5,g6)
    c: Coincident(g6,g7)
    c: Coincident(g7,g4)
    c: Horizontal(g4)
    c: Horizontal(g6)
    c: Vertical(g5)
    c: Vertical(g7)
    c: Coincident(g4,g-4)
    c: DistanceX(g-7,g4) = 6
    c: DistanceX(g-8,g2) = 6
    c: DistanceY(g5,g5) = 2
    c: DistanceY(g2,g2) = 2
FEATURE [PartDesign::Pad] Pad034
  BaseFeature = -> Pad033
  Direction = (0,0,1)
  Length = 8.2
  Length2 = 10
  Profile = -> Sketch052
  ReferenceAxis = -> Sketch052 [N_Axis]
  Refine = true
  Suppressed = false
  Type = 0
FEATURE [Sketcher::SketchObject] Sketch053
  ArcFitTolerance = 1e-06
  AttachmentSupport = -> [Pad034]
  ExternalGeometry = -> [Pad034]
  FullyConstrained = true
  MakeInternals = false
  MapMode = 5
  Placement = pos=(0,-11.75,0) rot=(1,0,0;1.5708rad)
  sketch-geometry (6):
    g0: LineSegment StartX=4.3 StartY=0 StartZ=0 EndX=4.3 EndY=-4.2 EndZ=0
    g1: LineSegment StartX=6.9 StartY=0 StartZ=0 EndX=6.9 EndY=-4.2 EndZ=0
    g2: ArcOfCircle CenterX=5.6 CenterY=-4.2 CenterZ=0 NormalX=0 NormalY=0 NormalZ=1 AngleXU=0 Radius=1.3 StartAngle=3.14159 EndAngle=6.28319
    g3: LineSegment [constr] StartX=4.3 StartY=-4.2 StartZ=0 EndX=6.9 EndY=-4.2 EndZ=0
    g4: LineSegment [constr] StartX=5.6 StartY=-4.2 StartZ=0 EndX=5.6 EndY=-5.5 EndZ=0
    g5: LineSegment StartX=6.9 StartY=0 StartZ=0 EndX=4.3 EndY=0 EndZ=0
  constraints (18):
    c: PointOnObject(g0,g-3)
    c: Vertical(g0)
    c: PointOnObject(g1,g-3)
    c: Vertical(g1)
    c: Coincident(g2,g0)
    c: Coincident(g2,g1)
    c: Coincident(g3,g0)
    c: Coincident(g3,g1)
    c: Horizontal(g3)
    c: PointOnObject(g2,g3)
    c: DistanceX(g0,g1) = 2.6
    c: DistanceX(g1,g-4) = 1.1
    c: Coincident(g4,g2)
    c: PointOnObject(g4,g2)
    c: Vertical(g4)
    c: DistanceY(g4,g0) = 5.5
    c: Coincident(g5,g1)
    c: Coincident(g5,g0)
FEATURE [PartDesign::Pocket] Pocket019
  BaseFeature = -> Pad034
  Direction = (0,1,-2e-16)
  Length = 2
  Length2 = 5
  Profile = -> Sketch053
  ReferenceAxis = -> Sketch053 [N_Axis]
  Refine = true
  Suppressed = false
  Type = 0
FEATURE [Sketcher::SketchObject] Sketch054
  ArcFitTolerance = 1e-06
  AttachmentSupport = -> [Pocket019]
  ExternalGeometry = -> [Pocket019]
  FullyConstrained = true
  MakeInternals = false
  MapMode = 5
  Placement = pos=(0,-20.5,0) rot=(0,0.707107,0.707107;3.14159rad)
  sketch-geometry (4):
    g0: LineSegment StartX=-6.9 StartY=0 StartZ=0 EndX=-4.3 EndY=0 EndZ=0
    g1: LineSegment StartX=-4.3 StartY=0 StartZ=0 EndX=-4.3 EndY=-4.2 EndZ=0
    g2: LineSegment StartX=-6.9 StartY=0 StartZ=0 EndX=-6.9 EndY=-4.2 EndZ=0
    g3: ArcOfCircle CenterX=-5.6 CenterY=-4.20001 CenterZ=0 NormalX=0 NormalY=0 NormalZ=1 AngleXU=0 Radius=1.3 StartAngle=3.14159 EndAngle=6.28319
  constraints (9):
    c: Coincident(g0,g-3)
    c: Coincident(g0,g-5)
    c: Coincident(g1,g0)
    c: Coincident(g1,g-5)
    c: Coincident(g2,g0)
    c: Coincident(g2,g-4)
    c: Coincident(g3,g2)
    c: Coincident(g3,g1)
    c: Tangent(g3,g-4)
FEATURE [PartDesign::Pocket] Pocket020
  BaseFeature = -> Pocket019
  Direction = (0,-1,2e-16)
  Length = 2
  Length2 = 5
  Profile = -> Sketch054
  ReferenceAxis = -> Sketch054 [N_Axis]
  Refine = true
  Suppressed = false
  Type = 0
FEATURE [Sketcher::SketchObject] Sketch055
  ArcFitTolerance = 1e-06
  AttachmentSupport = -> [Pocket020]
  ExternalGeometry = -> [Pocket020]
  FullyConstrained = true
  MakeInternals = false
  MapMode = 5
  Placement = pos=(0,0,0) rot=(0,0.707107,0.707107;3.14159rad)
  sketch-geometry (3):
    g0: LineSegment StartX=-2 StartY=-10.2 StartZ=0 EndX=-2 EndY=-8.9 EndZ=0
    g1: LineSegment StartX=-2 StartY=-10.2 StartZ=0 EndX=-6.8 EndY=-10.2 EndZ=0
    g2: LineSegment StartX=-2 StartY=-8.9 StartZ=0 EndX=-6.8 EndY=-10.2 EndZ=0
  constraints (7):
    c: Coincident(g0,g-4)
    c: PointOnObject(g0,g-3)
    c: DistanceY(g0,g0) = 1.3
    c: Coincident(g1,g0)
    c: Coincident(g2,g0)
    c: Coincident(g2,g1)
    c: Coincident(g-5,g1)
FEATURE [PartDesign::Pocket] Pocket021
  BaseFeature = -> Pocket020
  Direction = (0,-1,2e-16)
  Length = 32
  Length2 = 5
  Profile = -> Sketch055
  ReferenceAxis = -> Sketch055 [N_Axis]
  Refine = true
  Suppressed = false
  Type = 0
FEATURE [Sketcher::SketchObject] Sketch056
  ArcFitTolerance = 1e-06
  AttachmentSupport = -> [Pocket021]
  ExternalGeometry = -> [Pocket021]
  FullyConstrained = true
  MakeInternals = false
  MapMode = 5
  Placement = pos=(-2.10902,-1.7e-15,-7.78714) rot=(0.991268,0,-0.131859;3.14159rad)
  sketch-geometry (8):
    g0: LineSegment StartX=5.25705 StartY=31 StartZ=0 EndX=5.25705 EndY=21.5 EndZ=0
    g1: LineSegment StartX=5.25705 StartY=21.5 StartZ=0 EndX=8.22998 EndY=21.5 EndZ=0
    g2: LineSegment StartX=8.22998 StartY=21.5 StartZ=0 EndX=8.22998 EndY=31 EndZ=0
    g3: LineSegment StartX=8.22998 StartY=31 StartZ=0 EndX=5.25705 EndY=31 EndZ=0
    g4: LineSegment StartX=5.25705 StartY=10.75 StartZ=0 EndX=5.25705 EndY=1 EndZ=0
    g5: LineSegment StartX=5.25705 StartY=1 StartZ=0 EndX=8.22998 EndY=1 EndZ=0
    g6: LineSegment StartX=8.22998 StartY=1 StartZ=0 EndX=8.22998 EndY=10.75 EndZ=0
    g7: LineSegment StartX=8.22998 StartY=10.75 StartZ=0 EndX=5.25705 EndY=10.75 EndZ=0
  constraints (24):
    c: Coincident(g0,g1)
    c: Coincident(g1,g2)
    c: Coincident(g2,g3)
    c: Coincident(g3,g0)
    c: Vertical(g0)
    c: Vertical(g2)
    c: Horizontal(g1)
    c: Horizontal(g3)
    c: Coincident(g4,g5)
    c: Coincident(g5,g6)
    c: Coincident(g6,g7)
    c: Coincident(g7,g4)
    c: Vertical(g4)
    c: Vertical(g6)
    c: Horizontal(g5)
    c: Horizontal(g7)
    c: DistanceY(g0,g-6) = 1
    c: DistanceY(g-5,g0) = 1
    c: DistanceY(g4,g-3) = 1
    c: DistanceY(g-4,g4) = 1
    c: DistanceX(g-4,g4) = 1
    c: DistanceX(g5,g-4) = 1
    c: DistanceX(g-5,g0) = 1
    c: DistanceX(g1,g-5) = 1
FEATURE [PartDesign::Pocket] Pocket022
  BaseFeature = -> Pocket021
  Direction = (0.261415,0,0.965226)
  Length = 0.3
  Length2 = 5
  Profile = -> Sketch056
  ReferenceAxis = -> Sketch056 [N_Axis]
  Refine = true
  Suppressed = false
  Type = 0
FEATURE [Sketcher::SketchObject] Sketch057
  ArcFitTolerance = 1e-06
  AttachmentSupport = -> [Pocket022]
  ExternalGeometry = -> [Pocket022]
  FullyConstrained = true
  MakeInternals = false
  MapMode = 5
  Placement = pos=(-2.03059,0,-7.49757) rot=(0.991268,0,-0.131859;3.14159rad)
  sketch-geometry (32):
    g0: LineSegment StartX=5.55705 StartY=10.45 StartZ=0 EndX=5.55705 EndY=1.3 EndZ=0
    g1: LineSegment StartX=5.55705 StartY=1.3 StartZ=0 EndX=6.15705 EndY=1.3 EndZ=0
    g2: LineSegment StartX=6.15705 StartY=1.3 StartZ=0 EndX=6.15705 EndY=10.45 EndZ=0
    g3: LineSegment StartX=6.15705 StartY=10.45 StartZ=0 EndX=5.55705 EndY=10.45 EndZ=0
    g4: LineSegment StartX=6.45705 StartY=10.45 StartZ=0 EndX=6.45705 EndY=1.3 EndZ=0
    g5: LineSegment StartX=6.45705 StartY=1.3 StartZ=0 EndX=7.05705 EndY=1.3 EndZ=0
    g6: LineSegment StartX=7.05705 StartY=1.3 StartZ=0 EndX=7.05705 EndY=10.45 EndZ=0
    g7: LineSegment StartX=7.05705 StartY=10.45 StartZ=0 EndX=6.45705 EndY=10.45 EndZ=0
    g8: LineSegment StartX=7.35705 StartY=10.45 StartZ=0 EndX=7.35705 EndY=1.3 EndZ=0
    g9: LineSegment StartX=7.35705 StartY=1.3 StartZ=0 EndX=7.92998 EndY=1.3 EndZ=0
    g10: LineSegment StartX=7.92998 StartY=1.3 StartZ=0 EndX=7.92998 EndY=10.45 EndZ=0
    g11: LineSegment StartX=7.92998 StartY=10.45 StartZ=0 EndX=7.35705 EndY=10.45 EndZ=0
    g12: LineSegment [constr] StartX=6.15705 StartY=10.45 StartZ=0 EndX=6.45705 EndY=10.45 EndZ=0
    g13: LineSegment [constr] StartX=7.05705 StartY=10.45 StartZ=0 EndX=7.35705 EndY=10.45 EndZ=0
    g14: LineSegment [constr] StartX=6.15705 StartY=1.3 StartZ=0 EndX=6.45705 EndY=1.3 EndZ=0
    g15: LineSegment [constr] StartX=7.05705 StartY=1.3 StartZ=0 EndX=7.35705 EndY=1.3 EndZ=0
    g16: LineSegment StartX=5.55705 StartY=30.7 StartZ=0 EndX=5.55705 EndY=21.8 EndZ=0
    g17: LineSegment StartX=5.55705 StartY=21.8 StartZ=0 EndX=6.15705 EndY=21.8 EndZ=0
    g18: LineSegment StartX=6.15705 StartY=21.8 StartZ=0 EndX=6.15705 EndY=30.7 EndZ=0
    g19: LineSegment StartX=6.15705 StartY=30.7 StartZ=0 EndX=5.55705 EndY=30.7 EndZ=0
    g20: LineSegment StartX=6.45705 StartY=30.7 StartZ=0 EndX=6.45705 EndY=21.8 EndZ=0
    g21: LineSegment StartX=6.45705 StartY=21.8 StartZ=0 EndX=7.05705 EndY=21.8 EndZ=0
    g22: LineSegment StartX=7.05705 StartY=21.8 StartZ=0 EndX=7.05705 EndY=30.7 EndZ=0
    g23: LineSegment StartX=7.05705 StartY=30.7 StartZ=0 EndX=6.45705 EndY=30.7 EndZ=0
    g24: LineSegment StartX=7.35705 StartY=30.7 StartZ=0 EndX=7.35705 EndY=21.8 EndZ=0
    g25: LineSegment StartX=7.35705 StartY=21.8 StartZ=0 EndX=7.92998 EndY=21.8 EndZ=0
    g26: LineSegment StartX=7.92998 StartY=21.8 StartZ=0 EndX=7.92998 EndY=30.7 EndZ=0
    g27: LineSegment StartX=7.92998 StartY=30.7 StartZ=0 EndX=7.35705 EndY=30.7 EndZ=0
    g28: LineSegment [constr] StartX=6.45705 StartY=30.7 StartZ=0 EndX=6.15705 EndY=30.7 EndZ=0
    g29: LineSegment [constr] StartX=7.35705 StartY=30.7 StartZ=0 EndX=7.05705 EndY=30.7 EndZ=0
    g30: LineSegment [constr] StartX=6.45705 StartY=21.8 StartZ=0 EndX=6.15705 EndY=21.8 EndZ=0
    g31: LineSegment [constr] StartX=7.35705 StartY=21.8 StartZ=0 EndX=7.05705 EndY=21.8 EndZ=0
  constraints (90):
    c: Coincident(g0,g1)
    c: Coincident(g1,g2)
    c: Coincident(g2,g3)
    c: Coincident(g3,g0)
    c: Vertical(g0)
    c: Vertical(g2)
    c: Horizontal(g1)
    c: Horizontal(g3)
    c: Coincident(g4,g5)
    c: Coincident(g5,g6)
    c: Coincident(g6,g7)
    c: Coincident(g7,g4)
    c: Vertical(g4)
    c: Vertical(g6)
    c: Horizontal(g5)
    c: Horizontal(g7)
    c: Coincident(g8,g9)
    c: Coincident(g9,g10)
    c: Coincident(g10,g11)
    c: Coincident(g11,g8)
    c: Vertical(g8)
    c: Vertical(g10)
    c: Horizontal(g9)
    c: Horizontal(g11)
    c: DistanceX(g-3,g-3) = 2.97293
    c: DistanceX(g-3,g0) = 0.3
    c: DistanceX(g10,g-3) = 0.3
    c: DistanceX(g6,g8) = 0.3
    c: DistanceX(g2,g4) = 0.3
    c: DistanceX(g3,g3) = 0.6
    c: DistanceX(g7,g7) = 0.6
    c: DistanceX(g11,g11) = 0.572927
    c: DistanceY(g0,g-3) = 0.3
    c: Coincident(g12,g2)
    c: Coincident(g12,g4)
    c: Coincident(g13,g6)
    c: Coincident(g13,g8)
    c: Horizontal(g12)
    c: Horizontal(g13)
    c: Coincident(g14,g1)
    c: Coincident(g14,g4)
    c: Coincident(g15,g5)
    c: Coincident(g15,g8)
    c: Horizontal(g14)
    c: Horizontal(g15)
    c: DistanceY(g-4,g0) = 0.3
    c: Coincident(g16,g17)
    c: Coincident(g17,g18)
    c: Coincident(g18,g19)
    c: Coincident(g19,g16)
    c: Vertical(g16)
    c: Vertical(g18)
    c: Horizontal(g17)
    c: Horizontal(g19)
    c: Coincident(g20,g21)
    c: Coincident(g21,g22)
    c: Coincident(g22,g23)
    c: Coincident(g23,g20)
    c: Vertical(g20)
    c: Vertical(g22)
    c: Horizontal(g21)
    c: Horizontal(g23)
    c: Coincident(g24,g25)
    c: Coincident(g25,g26)
    c: Coincident(g26,g27)
    c: Coincident(g27,g24)
    c: Vertical(g24)
    c: Vertical(g26)
    c: Horizontal(g25)
    c: Horizontal(g27)
    c: Coincident(g28,g20)
    c: Coincident(g28,g18)
    c: Coincident(g29,g24)
    c: Coincident(g29,g22)
    c: Horizontal(g28)
    c: Horizontal(g29)
    c: Coincident(g30,g20)
    c: Coincident(g30,g17)
    c: Horizontal(g30)
    c: Coincident(g31,g24)
    c: Coincident(g31,g21)
    c: Horizontal(g31)
    c: DistanceX(g-5,g16) = 0.3
    c: DistanceX(g30,g30) = 0.3
    c: DistanceX(g31,g31) = 0.3
    c: DistanceX(g17,g17) = 0.6
    c: DistanceX(g21,g21) = 0.6
    c: DistanceY(g-5,g16) = 0.3
    c: DistanceY(g16,g-6) = 0.3
    c: DistanceX(g26,g-6) = 0.3
FEATURE [PartDesign::Pad] Pad035
  BaseFeature = -> Pocket022
  Direction = (-0.261415,0,-0.965226)
  Length = 0.3
  Length2 = 10
  Profile = -> Sketch057
  ReferenceAxis = -> Sketch057 [N_Axis]
  Refine = true
  Suppressed = false
  Type = 0
FEATURE [Sketcher::SketchObject] Sketch058
  ArcFitTolerance = 1e-06
  AttachmentSupport = -> [Pad035]
  ExternalGeometry = -> [Pad035]
  FullyConstrained = true
  MakeInternals = false
  MapMode = 5
  Placement = pos=(0,0,-8.2) rot=(0,0,1;0rad)
  sketch-geometry (1):
    g0: Circle CenterX=20.6 CenterY=-16.25 CenterZ=0 NormalX=0 NormalY=0 NormalZ=1 AngleXU=0 Radius=5.25
  constraints (4):
    c: Diameter(g0) = 10.5
    c: DistanceY(g-3,g-3) = 8.75
    c: DistanceY(g0,g-3) = 4.5
    c: DistanceX(g-3,g0) = 13.8
FEATURE [PartDesign::Pocket] Pocket023
  BaseFeature = -> Pad035
  Direction = (0,0,-1)
  Length = 5
  Length2 = 5
  Profile = -> Sketch058
  ReferenceAxis = -> Sketch058 [N_Axis]
  Refine = true
  Suppressed = false
  Type = 0
FEATURE [Sketcher::SketchObject] Sketch059
  ArcFitTolerance = 1e-06
  AttachmentSupport = -> [Pocket023]
  ExternalGeometry = -> [Pocket023]
  FullyConstrained = true
  MakeInternals = false
  MapMode = 5
  Placement = pos=(0,0,-10.2) rot=(1,0,0;3.14159rad)
  sketch-geometry (2):
    g0: Circle CenterX=29.5 CenterY=16.25 CenterZ=0 NormalX=0 NormalY=0 NormalZ=1 AngleXU=0 Radius=0.75
    g1: LineSegment [constr] StartX=20.6 StartY=16.25 StartZ=0 EndX=29.5 EndY=16.25 EndZ=0
  constraints (5):
    c: Radius(g0) = 0.75
    c: Coincident(g1,g-3)
    c: Coincident(g1,g0)
    c: Horizontal(g1)
    c: DistanceX(g1,g1) = 8.9
FEATURE [PartDesign::Pocket] Pocket024
  BaseFeature = -> Pocket023
  Direction = (0,0,1)
  Length = 5
  Length2 = 5
  Profile = -> Sketch059
  ReferenceAxis = -> Sketch059 [N_Axis]
  Refine = true
  Suppressed = false
  Type = 0
FEATURE [Sketcher::SketchObject] Sketch060
  ArcFitTolerance = 1e-06
  AttachmentSupport = -> [Pocket024]
  ExternalGeometry = -> [Pocket024]
  FullyConstrained = true
  MakeInternals = false
  MapMode = 5
  Placement = pos=(0,0,-8.2) rot=(0,0,1;0rad)
  sketch-geometry (2):
    g0: Circle CenterX=29.5 CenterY=-16.25 CenterZ=0 NormalX=0 NormalY=0 NormalZ=1 AngleXU=0 Radius=0.75
    g1: Circle CenterX=29.5 CenterY=-16.25 CenterZ=0 NormalX=0 NormalY=0 NormalZ=1 AngleXU=0 Radius=2
  constraints (4):
    c: Coincident(g0,g-3)
    c: Equal(g0,g-3)
    c: Coincident(g1,g0)
    c: Diameter(g1) = 4
FEATURE [PartDesign::Pad] Pad036
  BaseFeature = -> Pocket024
  Direction = (0,0,1)
  Length = 2
  Length2 = 10
  Profile = -> Sketch060
  ReferenceAxis = -> Sketch060 [N_Axis]
  Refine = true
  Suppressed = false
  Type = 0
FEATURE [Sketcher::SketchObject] Sketch061
  ArcFitTolerance = 1e-06
  AttachmentSupport = -> [Pad036]
  ExternalGeometry = -> [Pad036]
  FullyConstrained = true
  MakeInternals = false
  MapMode = 5
  Placement = pos=(0,0,-10.2) rot=(1,0,0;3.14159rad)
  sketch-geometry (9):
    g0: LineSegment StartX=34 StartY=18.85 StartZ=0 EndX=41 EndY=18.85 EndZ=0
    g1: LineSegment StartX=41 StartY=18.85 StartZ=0 EndX=41 EndY=13.65 EndZ=0
    g2: LineSegment StartX=41 StartY=13.65 StartZ=0 EndX=34 EndY=13.65 EndZ=0
    g3: LineSegment StartX=34 StartY=13.65 StartZ=0 EndX=34 EndY=14.35 EndZ=0
    g4: LineSegment StartX=34 StartY=14.35 StartZ=0 EndX=39.7 EndY=14.35 EndZ=0
    g5: LineSegment StartX=39.7 StartY=14.35 StartZ=0 EndX=39.7 EndY=18.15 EndZ=0
    g6: LineSegment StartX=39.7 StartY=18.15 StartZ=0 EndX=34 EndY=18.15 EndZ=0
    g7: LineSegment StartX=34 StartY=18.85 StartZ=0 EndX=34 EndY=18.15 EndZ=0
    g8: LineSegment [constr] StartX=34 StartY=18.15 StartZ=0 EndX=34 EndY=14.35 EndZ=0
  constraints (27):
    c: Horizontal(g0)
    c: Coincident(g1,g0)
    c: Vertical(g1)
    c: Coincident(g2,g1)
    c: Horizontal(g2)
    c: Coincident(g3,g2)
    c: Coincident(g4,g3)
    c: Horizontal(g4)
    c: Coincident(g5,g4)
    c: Vertical(g5)
    c: Coincident(g6,g5)
    c: Horizontal(g6)
    c: Coincident(g7,g0)
    c: Coincident(g7,g6)
    c: Vertical(g7)
    c: Vertical(g3)
    c: Coincident(g8,g6)
    c: Coincident(g8,g3)
    c: Vertical(g8)
    c: DistanceY(g8,g8) = 3.8
    c: DistanceY(g7,g7) = 0.7
    c: DistanceY(g3,g3) = 0.7
    c: DistanceX(g5,g0) = 1.3
    c: DistanceX(g0,g0) = 7
    c: DistanceY(g5,g5) = 3.8
    c: DistanceY(g-3,g5) = 1.9
    c: DistanceX(g-3,g6) = 4.5
FEATURE [PartDesign::Pocket] Pocket025
  BaseFeature = -> Pad036
  Direction = (0,0,1)
  Length = 5
  Length2 = 5
  Profile = -> Sketch061
  ReferenceAxis = -> Sketch061 [N_Axis]
  Refine = true
  Suppressed = false
  Type = 0
FEATURE [Sketcher::SketchObject] Sketch062
  ArcFitTolerance = 1e-06
  AttachmentSupport = -> [Pocket025]
  ExternalGeometry = -> [Pocket025]
  FullyConstrained = true
  MakeInternals = false
  MapMode = 5
  Placement = pos=(0,0,-8.2) rot=(0,0,1;0rad)
  sketch-geometry (2):
    g0: Circle CenterX=52.1 CenterY=-16 CenterZ=0 NormalX=0 NormalY=0 NormalZ=1 AngleXU=0 Radius=2.7
    g1: LineSegment [constr] StartX=52.1 StartY=-16 StartZ=0 EndX=54.8 EndY=-16 EndZ=0
  constraints (9):
    c: DistanceY(g-4,g-3) = 0.0862915
    c: DistanceY(g-4,g-3) = 5.74315
    c: DistanceY(g-7,g-6) = 13.6
    c: DistanceY(g0,g-6) = 6.8
    c: Radius(g0) = 2.7
    c: Coincident(g1,g0)
    c: PointOnObject(g1,g0)
    c: Horizontal(g1)
    c: DistanceX(g1,g-3) = 1
FEATURE [PartDesign::Pad] Pad037
  BaseFeature = -> Pocket025
  Direction = (0,0,1)
  Length = 6
  Length2 = 10
  Profile = -> Sketch062
  ReferenceAxis = -> Sketch062 [N_Axis]
  Refine = true
  Suppressed = false
  Type = 0
FEATURE [PartDesign::Fillet] Fillet002
  Base = -> Pad037 [Edge151]
  BaseFeature = -> Pad037
  Radius = 0.3
  Refine = true
  SupportTransform = false
  Suppressed = false
  UseAllEdges = false
FEATURE [Sketcher::SketchObject] Sketch063
  ArcFitTolerance = 1e-06
  AttachmentSupport = -> [Fillet002]
  ExternalGeometry = -> [Fillet002]
  FullyConstrained = true
  MakeInternals = false
  MapMode = 5
  Placement = pos=(0,0,-10.2) rot=(1,0,0;3.14159rad)
  sketch-geometry (1):
    g0: Circle CenterX=52.1 CenterY=16 CenterZ=0 NormalX=0 NormalY=0 NormalZ=1 AngleXU=0 Radius=0.75
  constraints (2):
    c: Coincident(g0,g-3)
    c: Radius(g0) = 0.75
FEATURE [PartDesign::Pocket] Pocket026
  BaseFeature = -> Fillet002
  Direction = (0,0,1)
  Length = 6
  Length2 = 5
  Profile = -> Sketch063
  ReferenceAxis = -> Sketch063 [N_Axis]
  Refine = true
  Suppressed = false
  Type = 0
FEATURE [Sketcher::SketchObject] Sketch064
  ArcFitTolerance = 1e-06
  AttachmentSupport = -> [Pocket026]
  ExternalGeometry = -> [Pocket026]
  FullyConstrained = true
  MakeInternals = false
  MapMode = 5
  Placement = pos=(0,-26,0) rot=(1,0,0;1.5708rad)
  sketch-geometry (3):
    g0: LineSegment StartX=3.5 StartY=1.6 StartZ=0 EndX=3 EndY=1.6 EndZ=0
    g1: LineSegment StartX=3.5 StartY=1.6 StartZ=0 EndX=3.5 EndY=1.1 EndZ=0
    g2: LineSegment StartX=3.5 StartY=1.1 StartZ=0 EndX=3 EndY=1.6 EndZ=0
  constraints (8):
    c: Coincident(g0,g-4)
    c: PointOnObject(g0,g-3)
    c: Coincident(g1,g0)
    c: PointOnObject(g1,g-4)
    c: Coincident(g2,g1)
    c: Coincident(g2,g0)
    c: DistanceX(g0,g0) = 0.5
    c: DistanceY(g1,g1) = 0.5
FEATURE [PartDesign::Pocket] Pocket027
  BaseFeature = -> Pocket026
  Direction = (0,1,-2e-16)
  Length = 20
  Length2 = 5
  Profile = -> Sketch064
  ReferenceAxis = -> Sketch064 [N_Axis]
  Refine = true
  Suppressed = false
  Type = 0
FEATURE [PartDesign::Body] Body001  label="Front_Torso"
  AllowCompound = false
  Group = -> [Binder,Sketch045,Pad029,Sketch046,Pocket017,Sketch047,Pad030,Fillet001,Sketch048,Pad031,Sketch049,Pocket018,Sketch050,Pad032,Sketch051,Pad033,Sketch052,Pad034,Sketch053,Pocket019,Sketch054,Pocket020,Sketch055,Pocket021,Sketch056,Pocket022,Sketch057,Pad035,Sketch058,Pocket023,Sketch059,Pocket024,Sketch060,Pad036,Sketch061,Pocket025,Sketch062,Pad037,Fillet002,Sketch063,Pocket026,Sketch064,Pocket027]
  Origin = -> Origin001
  Tip = -> Pocket027
